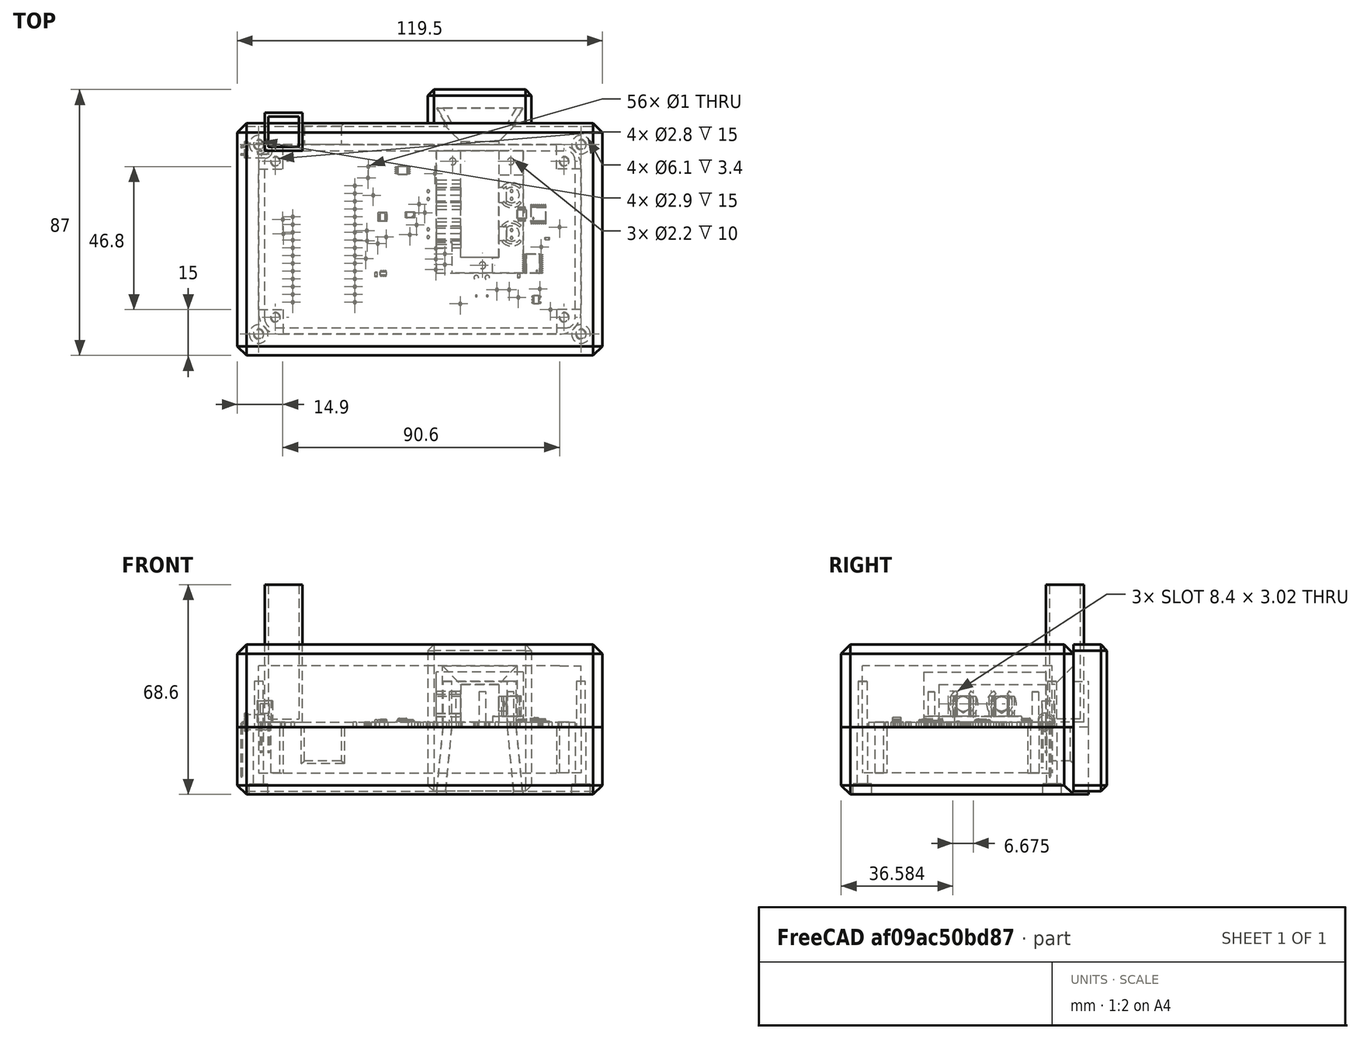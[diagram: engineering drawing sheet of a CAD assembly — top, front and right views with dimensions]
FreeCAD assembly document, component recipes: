
FREECAD ASSEMBLY — COMPONENT RECIPES ("phoenix-assembly")

This assembly document has 10 components, labeled P0..P9 below (a component is one placed body or linked part). 9 of them carry a construction recipe — the FreeCAD feature program that regenerates the part from scratch, quoted from this document or its linked companion documents; the rest are supplied as boundary geometry only. No exploded tour is included for this assembly.
COMPONENT P0 — geometry summary ("phoenix-main-board001"; no construction recipe available for this part):
  bounding box: 101.5 x 58.0 x 3.1 mm
  tessellated surface: 38,692 triangles
  volume: 9373 mm^3 (51% of its bounding box)
COMPONENT P1 — recipe-attached ("LED", modeled in this document).
Construction recipe (the document's own serialized feature program — sketch geometry with constraints, then the solid features built on it; lengths are millimeters unless a unit is written):

FEATURE [Sketcher::SketchObject] Sketch002
  ArcFitTolerance = 1e-06
  AttachmentSupport = -> [XY_Plane007]
  FullyConstrained = true
  MakeInternals = false
  MapMode = 5
  sketch-geometry (8):
    g0: LineSegment StartX=-2e-15 StartY=2.45 StartZ=0 EndX=-5.55 EndY=2.45 EndZ=0
    g1: LineSegment StartX=-5.55 StartY=2.45 StartZ=0 EndX=-5.55 EndY=3 EndZ=0
    g2: LineSegment StartX=-5.55 StartY=3 StartZ=0 EndX=-6.55 EndY=3 EndZ=0
    g3: LineSegment StartX=-6.55 StartY=3 StartZ=0 EndX=-6.55 EndY=0 EndZ=0
    g4: ArcOfCircle CenterX=0 CenterY=0 CenterZ=0 NormalX=0 NormalY=0 NormalZ=1 AngleXU=0 Radius=2.45 StartAngle=0 EndAngle=1.5708
    g5: LineSegment StartX=2.45 StartY=0 StartZ=0 EndX=-6.55 EndY=0 EndZ=0
    g6: GeomPoint X=0 Y=0 Z=0
    g7: LineSegment [constr] StartX=-5.55 StartY=2.45 StartZ=0 EndX=-5.55 EndY=0 EndZ=0
  constraints (22):
    c: PointOnObject(g0,g-2)
    c: Horizontal(g0)
    c: Coincident(g0,g1)
    c: Vertical(g1)
    c: Coincident(g1,g2)
    c: Horizontal(g2)
    c: Coincident(g2,g3)
    c: Vertical(g3)
    c: Coincident(g4,g-1)
    c: Coincident(g4,g0)
    c: Horizontal(g5)
    c: PointOnObject(g6,g5)
    c: Coincident(g6,g4)
    c: Coincident(g7,g0)
    c: Vertical(g7)
    c: DistanceX(g2,g2) = 1
    c: Coincident(g4,g5)
    c: PointOnObject(g7,g5)
    c: Coincident(g3,g5)
    c: DistanceX(g5,g5) = 9
    c: DistanceY(g3,g3) = 3
    c: DistanceY(g7,g7) = 2.45
FEATURE [PartDesign::Revolution] Revolution
  Angle = 360
  Angle2 = 60
  Axis = (1,0,0)
  Base = (0,0,0)
  Profile = -> Sketch002
  ReferenceAxis = -> X_Axis007
  Refine = true
  Reversed = true
  Suppressed = false
  Type = 0
FEATURE [Sketcher::SketchObject] Sketch003
  ArcFitTolerance = 1e-06
  AttachmentSupport = -> [Revolution]
  FullyConstrained = true
  MakeInternals = false
  MapMode = 5
  Placement = pos=(-6.55,0,0) rot=(0.57735,-0.57735,-0.57735;2.0944rad)
  sketch-geometry (9):
    g0: LineSegment StartX=-1.5 StartY=0.25 StartZ=0 EndX=-1.5 EndY=-0.25 EndZ=0
    g1: LineSegment StartX=-1.5 StartY=-0.25 StartZ=0 EndX=-1 EndY=-0.25 EndZ=0
    g2: LineSegment StartX=-1 StartY=-0.25 StartZ=0 EndX=-1 EndY=0.25 EndZ=0
    g3: LineSegment StartX=-1 StartY=0.25 StartZ=0 EndX=-1.5 EndY=0.25 EndZ=0
    g4: LineSegment StartX=1 StartY=0.25 StartZ=0 EndX=1 EndY=-0.25 EndZ=0
    g5: LineSegment StartX=1 StartY=-0.25 StartZ=0 EndX=1.5 EndY=-0.25 EndZ=0
    g6: LineSegment StartX=1.5 StartY=-0.25 StartZ=0 EndX=1.5 EndY=0.25 EndZ=0
    g7: LineSegment StartX=1.5 StartY=0.25 StartZ=0 EndX=1 EndY=0.25 EndZ=0
    g8: LineSegment [constr] StartX=-1 StartY=0.25 StartZ=0 EndX=1 EndY=0.25 EndZ=0
  constraints (25):
    c: Coincident(g0,g1)
    c: Coincident(g1,g2)
    c: Coincident(g2,g3)
    c: Coincident(g3,g0)
    c: Vertical(g0)
    c: Vertical(g2)
    c: Horizontal(g1)
    c: Horizontal(g3)
    c: Coincident(g4,g5)
    c: Coincident(g5,g6)
    c: Coincident(g6,g7)
    c: Coincident(g7,g4)
    c: Vertical(g4)
    c: Vertical(g6)
    c: Horizontal(g5)
    c: Horizontal(g7)
    c: DistanceX(g3,g3) = 0.5
    c: DistanceY(g0,g0) = 0.5
    c: Equal(g7,g3)
    c: Coincident(g8,g2)
    c: Coincident(g8,g4)
    c: Horizontal(g8)
    c: Equal(g4,g0)
    c: Symmetric(g2,g4,g-1)
    c: DistanceX(g8,g8) = 2
FEATURE [Sketcher::SketchObject] Sketch004
  ArcFitTolerance = 1e-06
  AttachmentSupport = -> [XZ_Plane007,Revolution]
  ExternalGeometry = -> [Revolution]
  FullyConstrained = true
  MakeInternals = false
  MapMode = 5
  Placement = pos=(0,0,0) rot=(1,0,0;1.5708rad)
  sketch-geometry (4):
    g0: LineSegment StartX=-6.55 StartY=-2e-16 StartZ=0 EndX=-6.65 EndY=-2e-16 EndZ=0
    g1: LineSegment StartX=-7.65 StartY=-1 StartZ=0 EndX=-7.65 EndY=-15 EndZ=0
    g2: ArcOfCircle CenterX=-6.65 CenterY=-1 CenterZ=0 NormalX=0 NormalY=0 NormalZ=1 AngleXU=0 Radius=1 StartAngle=1.5708 EndAngle=3.14159
    g3: GeomPoint [constr] X=-7.65 Y=0 Z=0
  constraints (10):
    c: Symmetric(g-3,g-3,g0)
    c: PointOnObject(g3,g-1)
    c: Vertical(g1)
    c: PointOnObject(g3,g0)
    c: PointOnObject(g3,g1)
    c: Tangent(g0,g2) = -1.5708
    c: Tangent(g1,g2) = -1.5708
    c: DistanceX(g0,g0) = 0.1
    c: DistanceX(g1,g0) = 1
    c: DistanceY(g1,g1) = 14
FEATURE [Sketcher::SketchObject] Sketch005
  ArcFitTolerance = 1e-06
  AttachmentSupport = -> [Revolution]
  ExternalGeometry = -> [Sketch003]
  FullyConstrained = true
  MakeInternals = false
  MapMode = 5
  Placement = pos=(-6.55,0,0) rot=(0.57735,-0.57735,-0.57735;2.0944rad)
  sketch-geometry (4):
    g0: LineSegment StartX=1 StartY=0.25 StartZ=0 EndX=1.5 EndY=0.25 EndZ=0
    g1: LineSegment StartX=1.5 StartY=-0.25 StartZ=0 EndX=1.5 EndY=0.25 EndZ=0
    g2: LineSegment StartX=1 StartY=0.25 StartZ=0 EndX=1 EndY=-0.25 EndZ=0
    g3: LineSegment StartX=1 StartY=-0.25 StartZ=0 EndX=1.5 EndY=-0.25 EndZ=0
  constraints (8):
    c: Coincident(g0,g-6)
    c: Coincident(g0,g-4)
    c: Coincident(g1,g-5)
    c: Coincident(g1,g0)
    c: Coincident(g2,g0)
    c: Coincident(g2,g-6)
    c: Coincident(g3,g2)
    c: Coincident(g3,g1)
FEATURE [PartDesign::AdditivePipe] AdditivePipe
  AuxilleryCurvelinear = true
  AuxillerySpineTangent = false
  BaseFeature = -> Revolution
  Binormal = (0,0,0)
  Mode = 0
  Profile = -> Sketch005
  Refine = true
  Spine = -> Sketch004
  SpineTangent = false
  Suppressed = false
  Transformation = 0
  Transition = 0
FEATURE [Sketcher::SketchObject] Sketch006
  ArcFitTolerance = 1e-06
  AttachmentSupport = -> [Revolution]
  ExternalGeometry = -> [Sketch003]
  FullyConstrained = true
  MakeInternals = false
  MapMode = 5
  Placement = pos=(-6.55,0,0) rot=(0.57735,-0.57735,-0.57735;2.0944rad)
  sketch-geometry (4):
    g0: LineSegment StartX=-1.5 StartY=0.25 StartZ=0 EndX=-1 EndY=0.25 EndZ=0
    g1: LineSegment StartX=-1 StartY=0.25 StartZ=0 EndX=-1 EndY=-0.25 EndZ=0
    g2: LineSegment StartX=-1 StartY=-0.25 StartZ=0 EndX=-1.5 EndY=-0.25 EndZ=0
    g3: LineSegment StartX=-1.5 StartY=-0.25 StartZ=0 EndX=-1.5 EndY=0.25 EndZ=0
  constraints (8):
    c: Coincident(g0,g-6)
    c: Coincident(g0,g-4)
    c: Coincident(g1,g0)
    c: Coincident(g1,g-5)
    c: Coincident(g2,g-5)
    c: Coincident(g2,g-6)
    c: Coincident(g3,g2)
    c: Coincident(g3,g0)
FEATURE [PartDesign::AdditivePipe] AdditivePipe001
  AuxilleryCurvelinear = true
  AuxillerySpineTangent = false
  BaseFeature = -> AdditivePipe
  Binormal = (0,0,0)
  Mode = 0
  Profile = -> Sketch006
  Refine = true
  Spine = -> Sketch004
  SpineTangent = false
  Suppressed = false
  Transformation = 0
  Transition = 0
FEATURE [PartDesign::Pad] Pad001
  BaseFeature = -> AdditivePipe001
  Direction = (0,0,-1)
  Length = 3
  Length2 = 10
  Profile = -> AdditivePipe001 [Face21]
  Refine = true
  Suppressed = false
  Type = 0
FEATURE [Sketcher::SketchObject] Sketch007
  ArcFitTolerance = 1e-06
  AttachmentSupport = -> [Pad001]
  ExternalGeometry = -> [Pad001]
  FullyConstrained = true
  MakeInternals = false
  MapMode = 5
  Placement = pos=(-5.55,0,0) rot=(0.57735,0.57735,0.57735;2.0944rad)
  sketch-geometry (3):
    g0: LineSegment StartX=-2.45 StartY=1.73133 StartZ=0 EndX=-2.45 EndY=-1.73133 EndZ=0
    g1: ArcOfCircle CenterX=-1.1943e-05 CenterY=5e-16 CenterZ=0 NormalX=0 NormalY=0 NormalZ=1 AngleXU=0 Radius=2.99999 StartAngle=2.52641 EndAngle=3.75678
    g2: GeomPoint X=-2.45 Y=2e-16 Z=0
  constraints (8):
    c: PointOnObject(g0,g-3)
    c: PointOnObject(g0,g-3)
    c: Vertical(g0)
    c: Coincident(g1,g0)
    c: Coincident(g1,g0)
    c: Symmetric(g0,g0,g2)
    c: PointOnObject(g2,g-4)
    c: Tangent(g1,g-3)
FEATURE [PartDesign::Pocket] Pocket
  BaseFeature = -> Pad001
  Direction = (-1,0,0)
  Length = 5
  Length2 = 5
  Profile = -> Sketch007
  ReferenceAxis = -> Sketch007 [N_Axis]
  Refine = true
  Suppressed = false
  Type = 0
FEATURE [PartDesign::Body] Body001
  AllowCompound = false
  Group = -> [Sketch002,Revolution,Sketch003,Sketch004,Sketch005,Sketch006,AdditivePipe,AdditivePipe001,Pad001,Sketch007,Pocket]
  Origin = -> Origin007
  Tip = -> Pocket
COMPONENT P2 — recipe-attached ("LED001", modeled in this document).
Construction recipe (the document's own serialized feature program — sketch geometry with constraints, then the solid features built on it; lengths are millimeters unless a unit is written):

FEATURE [Sketcher::SketchObject] Sketch008
  ArcFitTolerance = 1e-06
  AttachmentSupport = -> [XY_Plane009]
  FullyConstrained = true
  MakeInternals = false
  MapMode = 5
  sketch-geometry (8):
    g0: LineSegment StartX=-2e-15 StartY=2.45 StartZ=0 EndX=-5.55 EndY=2.45 EndZ=0
    g1: LineSegment StartX=-5.55 StartY=2.45 StartZ=0 EndX=-5.55 EndY=3 EndZ=0
    g2: LineSegment StartX=-5.55 StartY=3 StartZ=0 EndX=-6.55 EndY=3 EndZ=0
    g3: LineSegment StartX=-6.55 StartY=3 StartZ=0 EndX=-6.55 EndY=0 EndZ=0
    g4: ArcOfCircle CenterX=0 CenterY=0 CenterZ=0 NormalX=0 NormalY=0 NormalZ=1 AngleXU=0 Radius=2.45 StartAngle=0 EndAngle=1.5708
    g5: LineSegment StartX=2.45 StartY=0 StartZ=0 EndX=-6.55 EndY=0 EndZ=0
    g6: GeomPoint X=0 Y=0 Z=0
    g7: LineSegment [constr] StartX=-5.55 StartY=2.45 StartZ=0 EndX=-5.55 EndY=0 EndZ=0
  constraints (22):
    c: PointOnObject(g0,g-2)
    c: Horizontal(g0)
    c: Coincident(g0,g1)
    c: Vertical(g1)
    c: Coincident(g1,g2)
    c: Horizontal(g2)
    c: Coincident(g2,g3)
    c: Vertical(g3)
    c: Coincident(g4,g-1)
    c: Coincident(g4,g0)
    c: Horizontal(g5)
    c: PointOnObject(g6,g5)
    c: Coincident(g6,g4)
    c: Coincident(g7,g0)
    c: Vertical(g7)
    c: DistanceX(g2,g2) = 1
    c: Coincident(g4,g5)
    c: PointOnObject(g7,g5)
    c: Coincident(g3,g5)
    c: DistanceX(g5,g5) = 9
    c: DistanceY(g3,g3) = 3
    c: DistanceY(g7,g7) = 2.45
FEATURE [PartDesign::Revolution] Revolution001
  Angle = 360
  Angle2 = 60
  Axis = (1,0,0)
  Base = (0,0,0)
  Profile = -> Sketch008
  ReferenceAxis = -> X_Axis009
  Refine = true
  Reversed = true
  Suppressed = false
  Type = 0
FEATURE [Sketcher::SketchObject] Sketch009
  ArcFitTolerance = 1e-06
  AttachmentSupport = -> [Revolution001]
  FullyConstrained = true
  MakeInternals = false
  MapMode = 5
  Placement = pos=(-6.55,0,0) rot=(0.57735,-0.57735,-0.57735;2.0944rad)
  sketch-geometry (9):
    g0: LineSegment StartX=-1.5 StartY=0.25 StartZ=0 EndX=-1.5 EndY=-0.25 EndZ=0
    g1: LineSegment StartX=-1.5 StartY=-0.25 StartZ=0 EndX=-1 EndY=-0.25 EndZ=0
    g2: LineSegment StartX=-1 StartY=-0.25 StartZ=0 EndX=-1 EndY=0.25 EndZ=0
    g3: LineSegment StartX=-1 StartY=0.25 StartZ=0 EndX=-1.5 EndY=0.25 EndZ=0
    g4: LineSegment StartX=1 StartY=0.25 StartZ=0 EndX=1 EndY=-0.25 EndZ=0
    g5: LineSegment StartX=1 StartY=-0.25 StartZ=0 EndX=1.5 EndY=-0.25 EndZ=0
    g6: LineSegment StartX=1.5 StartY=-0.25 StartZ=0 EndX=1.5 EndY=0.25 EndZ=0
    g7: LineSegment StartX=1.5 StartY=0.25 StartZ=0 EndX=1 EndY=0.25 EndZ=0
    g8: LineSegment [constr] StartX=-1 StartY=0.25 StartZ=0 EndX=1 EndY=0.25 EndZ=0
  constraints (25):
    c: Coincident(g0,g1)
    c: Coincident(g1,g2)
    c: Coincident(g2,g3)
    c: Coincident(g3,g0)
    c: Vertical(g0)
    c: Vertical(g2)
    c: Horizontal(g1)
    c: Horizontal(g3)
    c: Coincident(g4,g5)
    c: Coincident(g5,g6)
    c: Coincident(g6,g7)
    c: Coincident(g7,g4)
    c: Vertical(g4)
    c: Vertical(g6)
    c: Horizontal(g5)
    c: Horizontal(g7)
    c: DistanceX(g3,g3) = 0.5
    c: DistanceY(g0,g0) = 0.5
    c: Equal(g7,g3)
    c: Coincident(g8,g2)
    c: Coincident(g8,g4)
    c: Horizontal(g8)
    c: Equal(g4,g0)
    c: Symmetric(g2,g4,g-1)
    c: DistanceX(g8,g8) = 2
FEATURE [Sketcher::SketchObject] Sketch010
  ArcFitTolerance = 1e-06
  AttachmentSupport = -> [XZ_Plane009,Revolution001]
  ExternalGeometry = -> [Revolution001]
  FullyConstrained = true
  MakeInternals = false
  MapMode = 5
  Placement = pos=(0,0,0) rot=(1,0,0;1.5708rad)
  sketch-geometry (4):
    g0: LineSegment StartX=-6.55 StartY=-2e-16 StartZ=0 EndX=-6.65 EndY=-2e-16 EndZ=0
    g1: LineSegment StartX=-7.65 StartY=-1 StartZ=0 EndX=-7.65 EndY=-15 EndZ=0
    g2: ArcOfCircle CenterX=-6.65 CenterY=-1 CenterZ=0 NormalX=0 NormalY=0 NormalZ=1 AngleXU=0 Radius=1 StartAngle=1.5708 EndAngle=3.14159
    g3: GeomPoint [constr] X=-7.65 Y=0 Z=0
  constraints (10):
    c: Symmetric(g-3,g-3,g0)
    c: PointOnObject(g3,g-1)
    c: Vertical(g1)
    c: PointOnObject(g3,g0)
    c: PointOnObject(g3,g1)
    c: Tangent(g0,g2) = -1.5708
    c: Tangent(g1,g2) = -1.5708
    c: DistanceX(g0,g0) = 0.1
    c: DistanceX(g1,g0) = 1
    c: DistanceY(g1,g1) = 14
FEATURE [Sketcher::SketchObject] Sketch011
  ArcFitTolerance = 1e-06
  AttachmentSupport = -> [Revolution001]
  ExternalGeometry = -> [Sketch009]
  FullyConstrained = true
  MakeInternals = false
  MapMode = 5
  Placement = pos=(-6.55,0,0) rot=(0.57735,-0.57735,-0.57735;2.0944rad)
  sketch-geometry (4):
    g0: LineSegment StartX=1 StartY=0.25 StartZ=0 EndX=1.5 EndY=0.25 EndZ=0
    g1: LineSegment StartX=1.5 StartY=-0.25 StartZ=0 EndX=1.5 EndY=0.25 EndZ=0
    g2: LineSegment StartX=1 StartY=0.25 StartZ=0 EndX=1 EndY=-0.25 EndZ=0
    g3: LineSegment StartX=1 StartY=-0.25 StartZ=0 EndX=1.5 EndY=-0.25 EndZ=0
  constraints (8):
    c: Coincident(g0,g-6)
    c: Coincident(g0,g-4)
    c: Coincident(g1,g-5)
    c: Coincident(g1,g0)
    c: Coincident(g2,g0)
    c: Coincident(g2,g-6)
    c: Coincident(g3,g2)
    c: Coincident(g3,g1)
FEATURE [PartDesign::AdditivePipe] AdditivePipe002
  AuxilleryCurvelinear = true
  AuxillerySpineTangent = false
  BaseFeature = -> Revolution001
  Binormal = (0,0,0)
  Mode = 0
  Profile = -> Sketch011
  Refine = true
  Spine = -> Sketch010
  SpineTangent = false
  Suppressed = false
  Transformation = 0
  Transition = 0
FEATURE [Sketcher::SketchObject] Sketch012
  ArcFitTolerance = 1e-06
  AttachmentSupport = -> [Revolution001]
  ExternalGeometry = -> [Sketch009]
  FullyConstrained = true
  MakeInternals = false
  MapMode = 5
  Placement = pos=(-6.55,0,0) rot=(0.57735,-0.57735,-0.57735;2.0944rad)
  sketch-geometry (4):
    g0: LineSegment StartX=-1.5 StartY=0.25 StartZ=0 EndX=-1 EndY=0.25 EndZ=0
    g1: LineSegment StartX=-1 StartY=0.25 StartZ=0 EndX=-1 EndY=-0.25 EndZ=0
    g2: LineSegment StartX=-1 StartY=-0.25 StartZ=0 EndX=-1.5 EndY=-0.25 EndZ=0
    g3: LineSegment StartX=-1.5 StartY=-0.25 StartZ=0 EndX=-1.5 EndY=0.25 EndZ=0
  constraints (8):
    c: Coincident(g0,g-6)
    c: Coincident(g0,g-4)
    c: Coincident(g1,g0)
    c: Coincident(g1,g-5)
    c: Coincident(g2,g-5)
    c: Coincident(g2,g-6)
    c: Coincident(g3,g2)
    c: Coincident(g3,g0)
FEATURE [PartDesign::AdditivePipe] AdditivePipe003
  AuxilleryCurvelinear = true
  AuxillerySpineTangent = false
  BaseFeature = -> AdditivePipe002
  Binormal = (0,0,0)
  Mode = 0
  Profile = -> Sketch012
  Refine = true
  Spine = -> Sketch010
  SpineTangent = false
  Suppressed = false
  Transformation = 0
  Transition = 0
FEATURE [PartDesign::Pad] Pad002
  BaseFeature = -> AdditivePipe003
  Direction = (0,0,-1)
  Length = 3
  Length2 = 10
  Profile = -> AdditivePipe003 [Face21]
  Refine = true
  Suppressed = false
  Type = 0
FEATURE [Sketcher::SketchObject] Sketch013
  ArcFitTolerance = 1e-06
  AttachmentSupport = -> [Pad002]
  ExternalGeometry = -> [Pad002]
  FullyConstrained = true
  MakeInternals = false
  MapMode = 5
  Placement = pos=(-5.55,0,0) rot=(0.57735,0.57735,0.57735;2.0944rad)
  sketch-geometry (3):
    g0: LineSegment StartX=-2.45 StartY=1.73133 StartZ=0 EndX=-2.45 EndY=-1.73133 EndZ=0
    g1: ArcOfCircle CenterX=-1.1943e-05 CenterY=5e-16 CenterZ=0 NormalX=0 NormalY=0 NormalZ=1 AngleXU=0 Radius=2.99999 StartAngle=2.52641 EndAngle=3.75678
    g2: GeomPoint X=-2.45 Y=2e-16 Z=0
  constraints (8):
    c: PointOnObject(g0,g-3)
    c: PointOnObject(g0,g-3)
    c: Vertical(g0)
    c: Coincident(g1,g0)
    c: Coincident(g1,g0)
    c: Symmetric(g0,g0,g2)
    c: PointOnObject(g2,g-4)
    c: Tangent(g1,g-3)
FEATURE [PartDesign::Pocket] Pocket001
  BaseFeature = -> Pad002
  Direction = (-1,0,0)
  Length = 5
  Length2 = 5
  Profile = -> Sketch013
  ReferenceAxis = -> Sketch013 [N_Axis]
  Refine = true
  Suppressed = false
  Type = 0
FEATURE [PartDesign::Body] Body002
  AllowCompound = false
  Group = -> [Sketch008,Revolution001,Sketch009,Sketch010,Sketch011,Sketch012,AdditivePipe002,AdditivePipe003,Pad002,Sketch013,Pocket001]
  Origin = -> Origin009
  Tip = -> Pocket001
COMPONENT P3 — recipe-attached ("Photodiode", modeled in this document).
Construction recipe (the document's own serialized feature program — sketch geometry with constraints, then the solid features built on it; lengths are millimeters unless a unit is written):

FEATURE [Sketcher::SketchObject] Sketch014
  ArcFitTolerance = 1e-06
  AttachmentSupport = -> [XY_Plane011]
  FullyConstrained = true
  MakeInternals = false
  MapMode = 5
  sketch-geometry (2):
    g0: ArcOfCircle CenterX=0 CenterY=0 CenterZ=0 NormalX=0 NormalY=0 NormalZ=1 AngleXU=0 Radius=2.5 StartAngle=5.78253 EndAngle=9.92543
    g1: LineSegment StartX=-2.19317 StartY=-1.2 StartZ=0 EndX=2.19317 EndY=-1.2 EndZ=0
  constraints (6):
    c: Coincident(g0,g-1)
    c: Diameter(g0) = 5
    c: Horizontal(g1)
    c: Distance(g0,g1) = -1.3
    c: Coincident(g0,g1)
    c: Coincident(g0,g1)
FEATURE [PartDesign::Pad] Pad003
  Direction = (0,0,1)
  Length = 7
  Length2 = 10
  Profile = -> Sketch014
  ReferenceAxis = -> Sketch014 [N_Axis]
  Refine = true
  Suppressed = false
  Type = 0
FEATURE [Sketcher::SketchObject] Sketch015
  ArcFitTolerance = 1e-06
  AttachmentSupport = -> [Pad003]
  FullyConstrained = true
  MakeInternals = false
  MapMode = 5
  Placement = pos=(0,0,0) rot=(1,0,0;3.14159rad)
  sketch-geometry (10):
    g0: LineSegment StartX=-1.5 StartY=0.25 StartZ=0 EndX=-1.5 EndY=-0.25 EndZ=0
    g1: LineSegment StartX=-1.5 StartY=-0.25 StartZ=0 EndX=-1 EndY=-0.25 EndZ=0
    g2: LineSegment StartX=-1 StartY=-0.25 StartZ=0 EndX=-1 EndY=0.25 EndZ=0
    g3: LineSegment StartX=-1 StartY=0.25 StartZ=0 EndX=-1.5 EndY=0.25 EndZ=0
    g4: LineSegment StartX=1 StartY=0.25 StartZ=0 EndX=1 EndY=-0.25 EndZ=0
    g5: LineSegment StartX=1 StartY=-0.25 StartZ=0 EndX=1.5 EndY=-0.25 EndZ=0
    g6: LineSegment StartX=1.5 StartY=-0.25 StartZ=0 EndX=1.5 EndY=0.25 EndZ=0
    g7: LineSegment StartX=1.5 StartY=0.25 StartZ=0 EndX=1 EndY=0.25 EndZ=0
    g8: GeomPoint X=-1 Y=0 Z=0
    g9: GeomPoint X=1 Y=0 Z=0
  constraints (25):
    c: Coincident(g0,g1)
    c: Coincident(g1,g2)
    c: Coincident(g2,g3)
    c: Coincident(g3,g0)
    c: Vertical(g0)
    c: Vertical(g2)
    c: Horizontal(g1)
    c: Horizontal(g3)
    c: Coincident(g4,g5)
    c: Coincident(g5,g6)
    c: Coincident(g6,g7)
    c: Coincident(g7,g4)
    c: Vertical(g4)
    c: Vertical(g6)
    c: Horizontal(g5)
    c: Horizontal(g7)
    c: Equal(g3,g2)
    c: Equal(g7,g6)
    c: Symmetric(g2,g2,g8)
    c: Symmetric(g4,g4,g9)
    c: Symmetric(g9,g8,g-1)
    c: PointOnObject(g9,g-1)
    c: DistanceX(g3,g3) = 0.5
    c: Equal(g3,g7)
    c: Distance(g4,g2) = 2
FEATURE [PartDesign::Pad] Pad004
  BaseFeature = -> Pad003
  Direction = (0,0,-1)
  Length = 10
  Length2 = 10
  Profile = -> Sketch015
  ReferenceAxis = -> Sketch015 [N_Axis]
  Refine = true
  Suppressed = false
  Type = 0
FEATURE [Sketcher::SketchObject] Sketch016
  ArcFitTolerance = 1e-06
  AttachmentSupport = -> [Pad004]
  ExternalGeometry = -> [Pad004]
  FullyConstrained = true
  MakeInternals = false
  MapMode = 5
  Placement = pos=(0,-1.2,0) rot=(1,0,0;1.5708rad)
  sketch-geometry (5):
    g0: LineSegment StartX=-1.5 StartY=6 StartZ=0 EndX=-1.5 EndY=3 EndZ=0
    g1: LineSegment StartX=-1.5 StartY=3 StartZ=0 EndX=1.5 EndY=3 EndZ=0
    g2: LineSegment StartX=1.5 StartY=3 StartZ=0 EndX=1.5 EndY=6 EndZ=0
    g3: LineSegment StartX=1.5 StartY=6 StartZ=0 EndX=-1.5 EndY=6 EndZ=0
    g4: GeomPoint X=0 Y=6 Z=0
  constraints (13):
    c: Coincident(g0,g1)
    c: Coincident(g1,g2)
    c: Coincident(g2,g3)
    c: Coincident(g3,g0)
    c: Vertical(g0)
    c: Vertical(g2)
    c: Horizontal(g1)
    c: Horizontal(g3)
    c: Symmetric(g3,g3,g4)
    c: PointOnObject(g4,g-2)
    c: DistanceX(g3,g3) = 3
    c: Equal(g2,g3)
    c: Distance(g-3,g3) = 1
FEATURE [PartDesign::Pocket] Pocket002
  BaseFeature = -> Pad004
  Direction = (0,1,-2e-16)
  Length = 0.1
  Length2 = 5
  Profile = -> Sketch016
  ReferenceAxis = -> Sketch016 [N_Axis]
  Refine = true
  Suppressed = false
  Type = 0
FEATURE [PartDesign::Body] Body003
  AllowCompound = false
  Group = -> [Sketch014,Pad003,Sketch015,Pad004,Sketch016,Pocket002]
  Origin = -> Origin011
  Tip = -> Pocket002
COMPONENT P4 — recipe-attached ("Photodiode001", modeled in this document).
Construction recipe (the document's own serialized feature program — sketch geometry with constraints, then the solid features built on it; lengths are millimeters unless a unit is written):

FEATURE [Sketcher::SketchObject] Sketch017
  ArcFitTolerance = 1e-06
  AttachmentSupport = -> [XY_Plane013]
  FullyConstrained = true
  MakeInternals = false
  MapMode = 5
  sketch-geometry (2):
    g0: ArcOfCircle CenterX=0 CenterY=0 CenterZ=0 NormalX=0 NormalY=0 NormalZ=1 AngleXU=0 Radius=2.5 StartAngle=5.78253 EndAngle=9.92543
    g1: LineSegment StartX=-2.19317 StartY=-1.2 StartZ=0 EndX=2.19317 EndY=-1.2 EndZ=0
  constraints (6):
    c: Coincident(g0,g-1)
    c: Diameter(g0) = 5
    c: Horizontal(g1)
    c: Distance(g0,g1) = -1.3
    c: Coincident(g0,g1)
    c: Coincident(g0,g1)
FEATURE [PartDesign::Pad] Pad005
  Direction = (0,0,1)
  Length = 7
  Length2 = 10
  Profile = -> Sketch017
  ReferenceAxis = -> Sketch017 [N_Axis]
  Refine = true
  Suppressed = false
  Type = 0
FEATURE [Sketcher::SketchObject] Sketch018
  ArcFitTolerance = 1e-06
  AttachmentSupport = -> [Pad005]
  FullyConstrained = true
  MakeInternals = false
  MapMode = 5
  Placement = pos=(0,0,0) rot=(1,0,0;3.14159rad)
  sketch-geometry (10):
    g0: LineSegment StartX=-1.5 StartY=0.25 StartZ=0 EndX=-1.5 EndY=-0.25 EndZ=0
    g1: LineSegment StartX=-1.5 StartY=-0.25 StartZ=0 EndX=-1 EndY=-0.25 EndZ=0
    g2: LineSegment StartX=-1 StartY=-0.25 StartZ=0 EndX=-1 EndY=0.25 EndZ=0
    g3: LineSegment StartX=-1 StartY=0.25 StartZ=0 EndX=-1.5 EndY=0.25 EndZ=0
    g4: LineSegment StartX=1 StartY=0.25 StartZ=0 EndX=1 EndY=-0.25 EndZ=0
    g5: LineSegment StartX=1 StartY=-0.25 StartZ=0 EndX=1.5 EndY=-0.25 EndZ=0
    g6: LineSegment StartX=1.5 StartY=-0.25 StartZ=0 EndX=1.5 EndY=0.25 EndZ=0
    g7: LineSegment StartX=1.5 StartY=0.25 StartZ=0 EndX=1 EndY=0.25 EndZ=0
    g8: GeomPoint X=-1 Y=0 Z=0
    g9: GeomPoint X=1 Y=0 Z=0
  constraints (25):
    c: Coincident(g0,g1)
    c: Coincident(g1,g2)
    c: Coincident(g2,g3)
    c: Coincident(g3,g0)
    c: Vertical(g0)
    c: Vertical(g2)
    c: Horizontal(g1)
    c: Horizontal(g3)
    c: Coincident(g4,g5)
    c: Coincident(g5,g6)
    c: Coincident(g6,g7)
    c: Coincident(g7,g4)
    c: Vertical(g4)
    c: Vertical(g6)
    c: Horizontal(g5)
    c: Horizontal(g7)
    c: Equal(g3,g2)
    c: Equal(g7,g6)
    c: Symmetric(g2,g2,g8)
    c: Symmetric(g4,g4,g9)
    c: Symmetric(g9,g8,g-1)
    c: PointOnObject(g9,g-1)
    c: DistanceX(g3,g3) = 0.5
    c: Equal(g3,g7)
    c: Distance(g4,g2) = 2
FEATURE [PartDesign::Pad] Pad006
  BaseFeature = -> Pad005
  Direction = (0,0,-1)
  Length = 10
  Length2 = 10
  Profile = -> Sketch018
  ReferenceAxis = -> Sketch018 [N_Axis]
  Refine = true
  Suppressed = false
  Type = 0
FEATURE [Sketcher::SketchObject] Sketch019
  ArcFitTolerance = 1e-06
  AttachmentSupport = -> [Pad006]
  ExternalGeometry = -> [Pad006]
  FullyConstrained = true
  MakeInternals = false
  MapMode = 5
  Placement = pos=(0,-1.2,0) rot=(1,0,0;1.5708rad)
  sketch-geometry (5):
    g0: LineSegment StartX=-1.5 StartY=6 StartZ=0 EndX=-1.5 EndY=3 EndZ=0
    g1: LineSegment StartX=-1.5 StartY=3 StartZ=0 EndX=1.5 EndY=3 EndZ=0
    g2: LineSegment StartX=1.5 StartY=3 StartZ=0 EndX=1.5 EndY=6 EndZ=0
    g3: LineSegment StartX=1.5 StartY=6 StartZ=0 EndX=-1.5 EndY=6 EndZ=0
    g4: GeomPoint X=0 Y=6 Z=0
  constraints (13):
    c: Coincident(g0,g1)
    c: Coincident(g1,g2)
    c: Coincident(g2,g3)
    c: Coincident(g3,g0)
    c: Vertical(g0)
    c: Vertical(g2)
    c: Horizontal(g1)
    c: Horizontal(g3)
    c: Symmetric(g3,g3,g4)
    c: PointOnObject(g4,g-2)
    c: DistanceX(g3,g3) = 3
    c: Equal(g2,g3)
    c: Distance(g-3,g3) = 1
FEATURE [PartDesign::Pocket] Pocket003
  BaseFeature = -> Pad006
  Direction = (0,1,-2e-16)
  Length = 0.1
  Length2 = 5
  Profile = -> Sketch019
  ReferenceAxis = -> Sketch019 [N_Axis]
  Refine = true
  Suppressed = false
  Type = 0
FEATURE [PartDesign::Body] Body004
  AllowCompound = false
  Group = -> [Sketch017,Pad005,Sketch018,Pad006,Sketch019,Pocket003]
  Origin = -> Origin013
  Tip = -> Pocket003
COMPONENT P5 — recipe-attached ("Cuvette", modeled in this document).
Construction recipe (the document's own serialized feature program — sketch geometry with constraints, then the solid features built on it; lengths are millimeters unless a unit is written):

FEATURE [Sketcher::SketchObject] Sketch020
  ArcFitTolerance = 1e-06
  AttachmentSupport = -> [XY_Plane015]
  FullyConstrained = true
  MakeInternals = false
  MapMode = 5
  sketch-geometry (4):
    g0: LineSegment StartX=0 StartY=0 StartZ=0 EndX=12.4 EndY=0 EndZ=0
    g1: LineSegment StartX=12.4 StartY=0 StartZ=0 EndX=12.4 EndY=12.4 EndZ=0
    g2: LineSegment StartX=12.4 StartY=12.4 StartZ=0 EndX=0 EndY=12.4 EndZ=0
    g3: LineSegment StartX=0 StartY=12.4 StartZ=0 EndX=0 EndY=0 EndZ=0
  constraints (11):
    c: Coincident(g0,g1)
    c: Coincident(g1,g2)
    c: Coincident(g2,g3)
    c: Coincident(g3,g0)
    c: Horizontal(g0)
    c: Horizontal(g2)
    c: Vertical(g1)
    c: Vertical(g3)
    c: Coincident(g0,g-1)
    c: DistanceX(g2,g2) = 12.4
    c: DistanceY(g3,g3) = 12.4
FEATURE [PartDesign::Pad] Pad007
  Direction = (0,0,1)
  Length = 45
  Length2 = 10
  Profile = -> Sketch020
  ReferenceAxis = -> Sketch020 [N_Axis]
  Refine = true
  Suppressed = false
  Type = 0
FEATURE [Sketcher::SketchObject] Sketch021
  ArcFitTolerance = 1e-06
  AttachmentSupport = -> [Pad007]
  ExternalGeometry = -> [Pad007]
  FullyConstrained = true
  MakeInternals = false
  MapMode = 5
  Placement = pos=(0,0,45) rot=(0,0,1;0rad)
  sketch-geometry (5):
    g0: LineSegment StartX=1.2 StartY=11.2 StartZ=0 EndX=1.2 EndY=1.2 EndZ=0
    g1: LineSegment StartX=1.2 StartY=1.2 StartZ=0 EndX=11.2 EndY=1.2 EndZ=0
    g2: LineSegment StartX=11.2 StartY=1.2 StartZ=0 EndX=11.2 EndY=11.2 EndZ=0
    g3: LineSegment StartX=11.2 StartY=11.2 StartZ=0 EndX=1.2 EndY=11.2 EndZ=0
    g4: GeomPoint X=6.2 Y=6.2 Z=0
  constraints (12):
    c: Coincident(g0,g1)
    c: Coincident(g1,g2)
    c: Coincident(g2,g3)
    c: Coincident(g3,g0)
    c: Vertical(g0)
    c: Vertical(g2)
    c: Horizontal(g1)
    c: Horizontal(g3)
    c: Symmetric(g0,g1,g4)
    c: Symmetric(g-3,g-1,g4)
    c: DistanceX(g3,g3) = 10
    c: DistanceY(g2,g2) = 10
FEATURE [PartDesign::Pocket] Pocket004
  BaseFeature = -> Pad007
  Direction = (0,0,-1)
  Length = 44
  Length2 = 5
  Profile = -> Sketch021
  ReferenceAxis = -> Sketch021 [N_Axis]
  Refine = true
  Suppressed = false
  Type = 0
FEATURE [PartDesign::Body] Body005  label="cuvette"
  AllowCompound = false
  Group = -> [Sketch020,Pad007,Sketch021,Pocket004]
  Origin = -> Origin015
  Tip = -> Pocket004
COMPONENT P6 — recipe-attached ("Shroud", modeled in this document).
Construction recipe (the document's own serialized feature program — sketch geometry with constraints, then the solid features built on it; lengths are millimeters unless a unit is written):

FEATURE [PartDesign::SubShapeBinder] Binder  label="Cuvette001"
  BindCopyOnChange = 0
  BindMode = 0
  ClaimChildren = false
  Context = -> Assembly [Part010.Body.Binder.]
  Fuse = false
  MakeFace = true
  OffsetFill = false
  OffsetIntersection = false
  OffsetJoinType = 0
  OffsetOpenResult = false
  PartialLoad = false
  Refine = true
  Relative = true
  Support = -> [Part009[Body005.Pocket004.Face1]]
  _Version = 2
FEATURE [PartDesign::SubShapeBinder] Binder001  label="PCB"
  BindCopyOnChange = 0
  BindMode = 0
  ClaimChildren = false
  Context = -> Assembly [Part010.Body.Binder001.]
  Fuse = false
  MakeFace = true
  OffsetFill = false
  OffsetIntersection = false
  OffsetJoinType = 0
  OffsetOpenResult = false
  PartialLoad = false
  Refine = true
  Relative = true
  Support = -> [Board_bfa0[Pcb_bfa0.Face84]]
  _Version = 2
FEATURE [PartDesign::SubShapeBinder] Binder002  label="LED1"
  BindCopyOnChange = 0
  BindMode = 0
  ClaimChildren = false
  Context = -> Assembly [Part010.Body.Binder002.]
  Fuse = false
  MakeFace = true
  OffsetFill = false
  OffsetIntersection = false
  OffsetJoinType = 0
  OffsetOpenResult = false
  PartialLoad = false
  Refine = true
  Relative = true
  Support = -> [Part[Body001.Pocket.Edge4]]
  _Version = 2
FEATURE [PartDesign::SubShapeBinder] Binder003  label="LED2"
  BindCopyOnChange = 0
  BindMode = 0
  ClaimChildren = false
  Context = -> Assembly [Part010.Body.Binder003.]
  Fuse = false
  MakeFace = true
  OffsetFill = false
  OffsetIntersection = false
  OffsetJoinType = 0
  OffsetOpenResult = false
  PartialLoad = false
  Refine = true
  Relative = true
  Support = -> [Part006[Body002.Pocket001.Edge4]]
  _Version = 2
FEATURE [PartDesign::SubShapeBinder] Binder004
  BindCopyOnChange = 0
  BindMode = 0
  ClaimChildren = false
  Context = -> Assembly [Part010.Body.Binder004.]
  Fuse = false
  MakeFace = true
  OffsetFill = false
  OffsetIntersection = false
  OffsetJoinType = 0
  OffsetOpenResult = false
  PartialLoad = false
  Refine = true
  Relative = true
  Support = -> [Part008[Body004.Pocket003.Face2]]
  _Version = 2
FEATURE [Sketcher::SketchObject] Sketch
  ArcFitTolerance = 1e-06
  AttachmentSupport = -> [Binder]
  ExternalGeometry = -> [Binder]
  FullyConstrained = true
  MakeInternals = false
  MapMode = 5
  Placement = pos=(0,0,12.4) rot=(0,0,1;0rad)
  sketch-geometry (6):
    g0: LineSegment StartX=56.1806 StartY=-40.0057 StartZ=0 EndX=84.5806 EndY=-40.0057 EndZ=0
    g1: LineSegment StartX=84.5806 StartY=-40.0057 StartZ=0 EndX=84.5806 EndY=0 EndZ=0
    g2: LineSegment StartX=84.5806 StartY=0 StartZ=0 EndX=56.1806 EndY=0 EndZ=0
    g3: LineSegment StartX=56.1806 StartY=0 StartZ=0 EndX=56.1806 EndY=-40.0057 EndZ=0
    g4: GeomPoint X=76.5806 Y=0 Z=0
    g5: GeomPoint X=64.1806 Y=0 Z=0
  constraints (16):
    c: Coincident(g0,g1)
    c: Coincident(g1,g2)
    c: Coincident(g2,g3)
    c: Coincident(g3,g0)
    c: Horizontal(g0)
    c: Horizontal(g2)
    c: Vertical(g1)
    c: Vertical(g3)
    c: PointOnObject(g1,g-1)
    c: PointOnObject(g4,g-5)
    c: PointOnObject(g5,g2)
    c: PointOnObject(g4,g2)
    c: PointOnObject(g5,g-3)
    c: DistanceX(g4,g1) = 8
    c: Distance(g5,g2) = 8
    c: Distance(g-4,g0) = 5
FEATURE [PartDesign::Pad] Pad
  Direction = (0,0,1)
  Length = 4
  Length2 = 10
  Profile = -> Sketch
  ReferenceAxis = -> Sketch [N_Axis]
  Refine = true
  Suppressed = false
  Type = 0
FEATURE [Sketcher::SketchObject] Sketch022
  ArcFitTolerance = 1e-06
  AttachmentSupport = -> [Pad]
  ExternalGeometry = -> [Binder,Pad]
  FullyConstrained = false
  MakeInternals = false
  MapMode = 5
  Placement = pos=(0,0,12.4) rot=(1,0,0;3.14159rad)
  sketch-geometry (9):
    g0: LineSegment StartX=56.1806 StartY=40.0057 StartZ=0 EndX=56.1806 EndY=0 EndZ=0
    g1: LineSegment StartX=56.1806 StartY=0 StartZ=0 EndX=64.1806 EndY=0 EndZ=0
    g2: LineSegment StartX=84.5806 StartY=0 StartZ=0 EndX=84.5806 EndY=40.0057 EndZ=0
    g3: LineSegment StartX=84.5806 StartY=40.0057 StartZ=0 EndX=56.1806 EndY=40.0057 EndZ=0
    g4: LineSegment StartX=76.6127 StartY=34.9943 StartZ=0 EndX=64.1806 EndY=34.9943 EndZ=0
    g5: LineSegment StartX=64.1806 StartY=34.9943 StartZ=0 EndX=64.1806 EndY=0 EndZ=0
    g6: LineSegment StartX=76.5806 StartY=0 StartZ=0 EndX=76.6127 EndY=0 EndZ=0
    g7: LineSegment StartX=76.6127 StartY=0 StartZ=0 EndX=76.6127 EndY=34.9943 EndZ=0
    g8: LineSegment StartX=76.5806 StartY=0 StartZ=0 EndX=84.5806 EndY=0 EndZ=0
  constraints (22):
    c: Coincident(g0,g1)
    c: Coincident(g8,g2)
    c: Coincident(g2,g3)
    c: Coincident(g3,g0)
    c: Vertical(g0)
    c: Vertical(g2)
    c: Horizontal(g1)
    c: Horizontal(g3)
    c: Coincident(g0,g-7)
    c: Coincident(g8,g-9)
    c: Coincident(g4,g5)
    c: Coincident(g6,g7)
    c: Coincident(g7,g4)
    c: Horizontal(g4)
    c: Horizontal(g6)
    c: Vertical(g5)
    c: Vertical(g7)
    c: Coincident(g4,g-5)
    c: PointOnObject(g5,g-3)
    c: Coincident(g1,g5)
    c: PointOnObject(g8,g-4)
    c: PointOnObject(g6,g8)
FEATURE [PartDesign::Pad] Pad008
  BaseFeature = -> Pad
  Direction = (0,0,-1)
  Length = 10
  Length2 = 10
  Profile = -> Sketch022
  ReferenceAxis = -> Sketch022 [N_Axis]
  Refine = true
  Suppressed = false
  Type = 3
  UpToFace = -> Binder001 [Face1]
FEATURE [Sketcher::SketchObject] Sketch023
  ArcFitTolerance = 1e-06
  AttachmentSupport = -> [Pad008]
  ExternalGeometry = -> [Binder003]
  FullyConstrained = false
  MakeInternals = false
  MapMode = 5
  Placement = pos=(56.1806,0,0) rot=(0.57735,-0.57735,-0.57735;2.0944rad)
  sketch-geometry (19):
    g0: ArcOfCircle CenterX=27.0787 CenterY=6 CenterZ=0 NormalX=0 NormalY=0 NormalZ=1 AngleXU=0 Radius=2.45 StartAngle=5.32325 EndAngle=10.3847
    g1: LineSegment StartX=25.6735 StartY=3.99308 StartZ=0 EndX=27.0787 EndY=3.0091 EndZ=0
    g2: LineSegment StartX=27.0787 StartY=3.0091 StartZ=0 EndX=28.484 EndY=3.99308 EndZ=0
    g3: LineSegment [constr] StartX=25.6735 StartY=3.99308 StartZ=0 EndX=28.484 EndY=3.99308 EndZ=0
    g4: Circle [constr] CenterX=27.0787 CenterY=6 CenterZ=0 NormalX=0 NormalY=0 NormalZ=1 AngleXU=0 Radius=3.65
    g5: Circle [constr] CenterX=27.0787 CenterY=6 CenterZ=0 NormalX=0 NormalY=0 NormalZ=1 AngleXU=0 Radius=4.85
    g6: ArcOfCircle CenterX=27.0787 CenterY=6 CenterZ=0 NormalX=0 NormalY=0 NormalZ=1 AngleXU=0 Radius=3.65 StartAngle=5.23599 EndAngle=7.33038
    g7: ArcOfCircle CenterX=27.0787 CenterY=6 CenterZ=0 NormalX=0 NormalY=0 NormalZ=1 AngleXU=0 Radius=4.85 StartAngle=5.23599 EndAngle=7.33038
    g8: LineSegment [constr] StartX=27.0787 StartY=6 StartZ=0 EndX=29.5037 EndY=1.79978 EndZ=0
    g9: LineSegment [constr] StartX=27.0787 StartY=6 StartZ=0 EndX=24.6537 EndY=1.79978 EndZ=0
    g10: LineSegment [constr] StartX=27.0787 StartY=6 StartZ=0 EndX=27.0787 EndY=1.15 EndZ=0
    g11: LineSegment [constr] StartX=27.0787 StartY=6 StartZ=0 EndX=29.5037 EndY=10.2002 EndZ=0
    g12: LineSegment [constr] StartX=27.0787 StartY=6 StartZ=0 EndX=24.6537 EndY=10.2002 EndZ=0
    g13: LineSegment StartX=29.5037 StartY=1.79978 StartZ=0 EndX=28.9037 EndY=2.83901 EndZ=0
    g14: LineSegment StartX=29.5037 StartY=10.2002 StartZ=0 EndX=28.9037 EndY=9.16099 EndZ=0
    g15: LineSegment StartX=24.6537 StartY=10.2002 StartZ=0 EndX=25.2537 EndY=9.16099 EndZ=0
    g16: LineSegment StartX=24.6537 StartY=1.79978 StartZ=0 EndX=25.2537 EndY=2.83901 EndZ=0
    g17: ArcOfCircle CenterX=27.0787 CenterY=6 CenterZ=0 NormalX=0 NormalY=0 NormalZ=1 AngleXU=0 Radius=3.65 StartAngle=2.0944 EndAngle=4.18879
    g18: ArcOfCircle CenterX=27.0787 CenterY=6 CenterZ=0 NormalX=0 NormalY=0 NormalZ=1 AngleXU=0 Radius=4.85 StartAngle=2.0944 EndAngle=4.18879
  constraints (51):
    c: Coincident(g0,g-3)
    c: Coincident(g2,g1)
    c: Vertical(g1,g0)
    c: Coincident(g3,g1)
    c: Coincident(g3,g2)
    c: Angle(g1,g3) = 0.610865
    c: Tangent(g0,g1) = -1.5708
    c: Tangent(g0,g2) = -1.5708
    c: Radius(g0) = 2.45
    c: Coincident(g4,g0)
    c: Coincident(g5,g0)
    c: Distance(g0,g4) = 1.2
    c: Distance(g5,g4) = 1.2
    c: Coincident(g6,g0)
    c: Coincident(g7,g0)
    c: Equal(g4,g6)
    c: Equal(g7,g5)
    c: Coincident(g8,g0)
    c: Coincident(g9,g0)
    c: Coincident(g10,g0)
    c: Vertical(g10)
    c: Coincident(g11,g0)
    c: Coincident(g12,g0)
    c: PointOnObject(g12,g18)
    c: Angle(g9,g10) = 0.523599
    c: Angle(g10,g8) = 0.523599
    c: Angle(g12,g10) = 2.61799
    c: Angle(g10,g11) = 2.61799
    c: Coincident(g13,g8)
    c: Coincident(g14,g11)
    c: PointOnObject(g14,g6)
    c: Coincident(g15,g12)
    c: PointOnObject(g15,g17)
    c: Coincident(g16,g9)
    c: PointOnObject(g16,g17)
    c: PointOnObject(g16,g9)
    c: PointOnObject(g13,g8)
    c: PointOnObject(g14,g11)
    c: PointOnObject(g15,g12)
    c: Coincident(g7,g8)
    c: Coincident(g6,g13)
    c: Coincident(g18,g9)
    c: PointOnObject(g17,g9)
    c: Equal(g6,g17)
    c: PointOnObject(g6,g11)
    c: PointOnObject(g17,g15)
    c: Coincident(g6,g17)
    c: Equal(g7,g18)
    c: Coincident(g7,g11)
    c: PointOnObject(g18,g12)
    c: Coincident(g7,g18)
FEATURE [Sketcher::SketchObject] Sketch024
  ArcFitTolerance = 1e-06
  AttachmentSupport = -> [Pad008]
  ExternalGeometry = -> [Binder002,Binder003]
  FullyConstrained = true
  MakeInternals = false
  MapMode = 5
  Placement = pos=(56.1806,0,0) rot=(0.57735,-0.57735,-0.57735;2.0944rad)
  sketch-geometry (4):
    g0: LineSegment StartX=14.5251 StartY=6 StartZ=0 EndX=27.0787 EndY=6 EndZ=0
    g1: LineSegment StartX=20.8019 StartY=11 StartZ=0 EndX=20.8019 EndY=1 EndZ=0
    g2: GeomPoint [constr] X=20.8019 Y=6 Z=0
    g3: GeomPoint [constr] X=20.8019 Y=6 Z=0
  constraints (7):
    c: Coincident(g0,g-3)
    c: Coincident(g0,g-4)
    c: Vertical(g1)
    c: Symmetric(g0,g0,g2)
    c: Symmetric(g1,g1,g3)
    c: Coincident(g3,g2)
    c: DistanceY(g1,g1) = 10
FEATURE [PartDesign::Plane] DatumPlane
  AttachmentSupport = -> [Sketch024]
  Length = 124.385
  MapMode = 7
  Placement = pos=(56.1806,-20.8019,6) rot=(0,0.707107,0.707107;3.14159rad)
  ResizeMode = 0
  Width = 64.8041
FEATURE [PartDesign::Pocket] Pocket005  label="LED Hole"
  BaseFeature = -> Pad008
  Direction = (1,0,0)
  Length = 5
  Length2 = 5
  Profile = -> Sketch023
  ReferenceAxis = -> Sketch023 [N_Axis]
  Refine = true
  Suppressed = false
  Type = 2
FEATURE [PartDesign::Mirrored] Mirrored  label="LED Hole Mirror"
  BaseFeature = -> Pocket005
  MirrorPlane = -> DatumPlane
  Originals = -> [Pocket005]
  Refine = true
  Suppressed = false
  TransformMode = 0
FEATURE [PartDesign::SubShapeBinder] Binder007
  BindCopyOnChange = 0
  BindMode = 0
  ClaimChildren = false
  Context = -> Assembly [Part010.Body.Binder007.]
  Fuse = false
  MakeFace = true
  OffsetFill = false
  OffsetIntersection = false
  OffsetJoinType = 0
  OffsetOpenResult = false
  PartialLoad = false
  Refine = true
  Relative = true
  Support = -> [Part008[Body004.Pocket003.Face4]]
  _Version = 2
FEATURE [Sketcher::SketchObject] Sketch025
  ArcFitTolerance = 1e-06
  AttachmentSupport = -> [Mirrored]
  ExternalGeometry = -> [Binder007,Binder004]
  FullyConstrained = true
  MakeInternals = false
  MapMode = 5
  Placement = pos=(0,0,0) rot=(1,0,0;3.14159rad)
  sketch-geometry (17):
    g0: ArcOfCircle CenterX=80.7939 CenterY=14.5071 CenterZ=0 NormalX=0 NormalY=0 NormalZ=1 AngleXU=0 Radius=2.5 StartAngle=4.01697 EndAngle=8.54756
    g1: LineSegment StartX=79.1957 StartY=16.4295 StartZ=0 EndX=79.1922 EndY=12.5876 EndZ=0
    g2: Circle [constr] CenterX=80.7939 CenterY=14.5071 CenterZ=0 NormalX=0 NormalY=0 NormalZ=1 AngleXU=0 Radius=3.3
    g3: Circle [constr] CenterX=80.7939 CenterY=14.5071 CenterZ=0 NormalX=0 NormalY=0 NormalZ=1 AngleXU=0 Radius=4.1
    g4: ArcOfCircle CenterX=80.7939 CenterY=14.5071 CenterZ=0 NormalX=0 NormalY=0 NormalZ=1 AngleXU=0 Radius=3.3 StartAngle=3.83972 EndAngle=5.58505
    g5: ArcOfCircle CenterX=80.7939 CenterY=14.5071 CenterZ=0 NormalX=0 NormalY=0 NormalZ=1 AngleXU=0 Radius=4.1 StartAngle=3.83972 EndAngle=5.58505
    g6: LineSegment [constr] StartX=80.7939 StartY=14.5071 StartZ=0 EndX=76.6939 EndY=14.5071 EndZ=0
    g7: LineSegment [constr] StartX=80.7939 StartY=14.5071 StartZ=0 EndX=77.6531 EndY=17.1425 EndZ=0
    g8: LineSegment [constr] StartX=80.7939 StartY=14.5071 StartZ=0 EndX=83.9347 EndY=17.1425 EndZ=0
    g9: LineSegment [constr] StartX=80.7939 StartY=14.5071 StartZ=0 EndX=77.6531 EndY=11.8717 EndZ=0
    g10: LineSegment [constr] StartX=80.7939 StartY=14.5071 StartZ=0 EndX=83.9347 EndY=11.8717 EndZ=0
    g11: LineSegment StartX=77.6531 StartY=17.1425 StartZ=0 EndX=78.266 EndY=16.6283 EndZ=0
    g12: LineSegment StartX=83.9347 StartY=17.1425 StartZ=0 EndX=83.3219 EndY=16.6283 EndZ=0
    g13: LineSegment StartX=83.9347 StartY=11.8717 StartZ=0 EndX=83.3219 EndY=12.3859 EndZ=0
    g14: LineSegment StartX=77.6531 StartY=11.8717 StartZ=0 EndX=78.266 EndY=12.3859 EndZ=0
    g15: ArcOfCircle CenterX=80.7939 CenterY=14.5071 CenterZ=0 NormalX=0 NormalY=0 NormalZ=1 AngleXU=0 Radius=3.3 StartAngle=0.698132 EndAngle=2.44346
    g16: ArcOfCircle CenterX=80.7939 CenterY=14.5071 CenterZ=0 NormalX=0 NormalY=0 NormalZ=1 AngleXU=0 Radius=4.1 StartAngle=0.698132 EndAngle=2.44346
  constraints (49):
    c: Coincident(g0,g-3)
    c: Equal(g0,g-3)
    c: Parallel(g1,g-4)
    c: Distance(g1,g-4) = 0.4
    c: Coincident(g0,g1)
    c: Coincident(g0,g1)
    c: Coincident(g2,g0)
    c: Coincident(g3,g2)
    c: Coincident(g4,g2)
    c: Coincident(g5,g2)
    c: Distance(g0,g2) = 0.8
    c: Distance(g2,g3) = 0.8
    c: Coincident(g6,g0)
    c: Horizontal(g6)
    c: Coincident(g7,g0)
    c: Coincident(g8,g7)
    c: PointOnObject(g8,g16)
    c: Coincident(g9,g7)
    c: Coincident(g10,g7)
    c: Coincident(g11,g7)
    c: Coincident(g12,g8)
    c: PointOnObject(g12,g15)
    c: Coincident(g13,g10)
    c: PointOnObject(g13,g4)
    c: PointOnObject(g14,g4)
    c: Coincident(g14,g9)
    c: PointOnObject(g14,g9)
    c: PointOnObject(g13,g10)
    c: PointOnObject(g12,g8)
    c: PointOnObject(g11,g7)
    c: Angle(g7,g6) = 0.698132
    c: Angle(g6,g9) = 0.698132
    c: Angle(g8,g6) = 2.44346
    c: Angle(g6,g10) = 2.44346
    c: Coincident(g16,g7)
    c: Coincident(g15,g11)
    c: PointOnObject(g4,g9)
    c: Coincident(g5,g9)
    c: Equal(g4,g15)
    c: PointOnObject(g15,g8)
    c: Coincident(g4,g15)
    c: Equal(g5,g16)
    c: PointOnObject(g16,g8)
    c: Coincident(g5,g16)
    c: Coincident(g5,g10)
    c: PointOnObject(g4,g10)
    c: Equal(g16,g3)
    c: Equal(g15,g2)
    c: PointOnObject(g6,g3)
FEATURE [PartDesign::Pocket] Pocket006  label="PD Hole1"
  BaseFeature = -> Mirrored
  Direction = (0,0,1)
  Length = 0
  Length2 = 5
  Profile = -> Sketch025
  ReferenceAxis = -> Sketch025 [N_Axis]
  Refine = true
  Suppressed = false
  Type = 3
  UpToFace = -> Binder007 [Face1]
FEATURE [Sketcher::SketchObject] Sketch026
  ArcFitTolerance = 1e-06
  AttachmentSupport = -> [Pocket006]
  ExternalGeometry = -> [Binder004]
  FullyConstrained = true
  MakeInternals = false
  MapMode = 5
  Placement = pos=(76.6127,0,0) rot=(0.57735,-0.57735,-0.57735;2.0944rad)
  sketch-geometry (3):
    g0: LineSegment [constr] StartX=13.0082 StartY=7.5 StartZ=0 EndX=16.0082 EndY=4.5 EndZ=0
    g1: GeomPoint X=14.5082 Y=6 Z=0
    g2: Circle CenterX=14.5082 CenterY=6 CenterZ=0 NormalX=0 NormalY=0 NormalZ=1 AngleXU=0 Radius=2.37132
  constraints (5):
    c: Coincident(g0,g-5)
    c: Coincident(g0,g-6)
    c: Symmetric(g0,g0,g1)
    c: Coincident(g2,g1)
    c: Distance(g0,g2) = 0.25
FEATURE [PartDesign::Pocket] Pocket007  label="PD Hole2"
  BaseFeature = -> Pocket006
  Direction = (1,0,0)
  Length = 0
  Length2 = 5
  Profile = -> Sketch026
  ReferenceAxis = -> Sketch026 [N_Axis]
  Refine = true
  Suppressed = false
  Type = 3
  UpToFace = -> Pocket006 [Face34]
FEATURE [PartDesign::Mirrored] Mirrored001  label="PD Mirror"
  BaseFeature = -> Pocket007
  MirrorPlane = -> DatumPlane
  Originals = -> [Pocket006,Pocket007]
  Refine = true
  Suppressed = false
  TransformMode = 0
FEATURE [Sketcher::SketchObject] Sketch027
  ArcFitTolerance = 1e-06
  AttachmentSupport = -> [Mirrored001]
  ExternalGeometry = -> [Binder001]
  FullyConstrained = true
  MakeInternals = false
  MapMode = 5
  Placement = pos=(0,0,0) rot=(1,0,0;3.14159rad)
  sketch-geometry (3):
    g0: Circle CenterX=71.25 CenterY=37.5 CenterZ=0 NormalX=0 NormalY=0 NormalZ=1 AngleXU=0 Radius=1.1
    g1: Circle CenterX=80.5 CenterY=3.5 CenterZ=0 NormalX=0 NormalY=0 NormalZ=1 AngleXU=0 Radius=1.1
    g2: Circle CenterX=61.5 CenterY=3.5 CenterZ=0 NormalX=0 NormalY=0 NormalZ=1 AngleXU=0 Radius=1.1
  constraints (6):
    c: Coincident(g0,g-3)
    c: Equal(g0,g-3)
    c: Coincident(g1,g-5)
    c: Equal(g1,g-5)
    c: Coincident(g2,g-4)
    c: Equal(g2,g-4)
FEATURE [PartDesign::Pocket] Pocket008
  BaseFeature = -> Mirrored001
  Direction = (0,0,1)
  Length = 10
  Length2 = 5
  Profile = -> Sketch027
  ReferenceAxis = -> Sketch027 [N_Axis]
  Refine = true
  Suppressed = false
  Type = 0
FEATURE [Sketcher::SketchObject] Sketch028
  ArcFitTolerance = 1e-06
  AttachmentSupport = -> [Pocket008]
  ExternalGeometry = -> [Pocket008]
  FullyConstrained = true
  MakeInternals = false
  MapMode = 5
  Placement = pos=(84.5806,0,0) rot=(0.57735,0.57735,0.57735;2.0944rad)
  sketch-geometry (4):
    g0: LineSegment StartX=-40.0057 StartY=0 StartZ=0 EndX=-8.00566 EndY=0 EndZ=0
    g1: LineSegment StartX=-8.00566 StartY=0 StartZ=0 EndX=-8.00566 EndY=2 EndZ=0
    g2: LineSegment StartX=-8.00566 StartY=2 StartZ=0 EndX=-40.0057 EndY=2 EndZ=0
    g3: LineSegment StartX=-40.0057 StartY=2 StartZ=0 EndX=-40.0057 EndY=0 EndZ=0
  constraints (11):
    c: Coincident(g0,g1)
    c: Coincident(g1,g2)
    c: Coincident(g2,g3)
    c: Coincident(g3,g0)
    c: Horizontal(g0)
    c: Horizontal(g2)
    c: Vertical(g1)
    c: Vertical(g3)
    c: Coincident(g0,g-3)
    c: DistanceX(g2,g2) = 32
    c: DistanceY(g1,g1) = 2
FEATURE [PartDesign::Pocket] Pocket009
  BaseFeature = -> Pocket008
  Direction = (-1,0,0)
  Length = 10
  Length2 = 5
  Profile = -> Sketch028
  ReferenceAxis = -> Sketch028 [N_Axis]
  Refine = true
  Suppressed = false
  Type = 0
FEATURE [Sketcher::SketchObject] Sketch029
  ArcFitTolerance = 1e-06
  AttachmentSupport = -> [Pocket009]
  ExternalGeometry = -> [Pocket009]
  FullyConstrained = true
  MakeInternals = false
  MapMode = 5
  Placement = pos=(56.1806,0,0) rot=(0.57735,-0.57735,-0.57735;2.0944rad)
  sketch-geometry (4):
    g0: LineSegment StartX=40.0057 StartY=0 StartZ=0 EndX=40.0057 EndY=2 EndZ=0
    g1: LineSegment StartX=40.0057 StartY=2 StartZ=0 EndX=30.0057 EndY=2 EndZ=0
    g2: LineSegment StartX=30.0057 StartY=2 StartZ=0 EndX=30.0057 EndY=0 EndZ=0
    g3: LineSegment StartX=30.0057 StartY=0 StartZ=0 EndX=40.0057 EndY=0 EndZ=0
  constraints (11):
    c: Coincident(g0,g1)
    c: Coincident(g1,g2)
    c: Coincident(g2,g3)
    c: Coincident(g3,g0)
    c: Vertical(g0)
    c: Vertical(g2)
    c: Horizontal(g1)
    c: Horizontal(g3)
    c: Coincident(g0,g-3)
    c: DistanceX(g1,g1) = 10
    c: Distance(g2,g2) = 2
FEATURE [PartDesign::Pocket] Pocket010  label="ReliefSPI"
  BaseFeature = -> Pocket009
  Direction = (1,0,0)
  Length = 5
  Length2 = 5
  Profile = -> Sketch029
  ReferenceAxis = -> Sketch029 [N_Axis]
  Refine = true
  Suppressed = false
  Type = 0
FEATURE [PartDesign::Body] Body
  AllowCompound = false
  Group = -> [Binder,Binder001,Binder002,Binder003,Binder004,Binder007,Sketch,Pad,Sketch022,Pad008,Sketch023,Sketch024,DatumPlane,Pocket005,Mirrored,Sketch025,Pocket006,Sketch026,Pocket007,Mirrored001,Sketch027,Pocket008,Sketch028,Pocket009,Sketch029,Pocket010]
  Origin = -> Origin018
  Tip = -> Pocket010
COMPONENT P7 — recipe-attached ("Enclosure Back", modeled in this document).
Construction recipe (the document's own serialized feature program — sketch geometry with constraints, then the solid features built on it; lengths are millimeters unless a unit is written):

FEATURE [PartDesign::SubShapeBinder] Binder008
  BindCopyOnChange = 0
  BindMode = 0
  ClaimChildren = false
  Context = -> Assembly [Part011.Body006.Binder008.]
  Fuse = false
  MakeFace = true
  OffsetFill = false
  OffsetIntersection = false
  OffsetJoinType = 0
  OffsetOpenResult = false
  PartialLoad = false
  Refine = true
  Relative = true
  Support = -> [Board_bfa0[Pcb_bfa0.Face85]]
  _Version = 2
FEATURE [PartDesign::SubShapeBinder] Binder009
  BindCopyOnChange = 0
  BindMode = 0
  ClaimChildren = false
  Context = -> Assembly [Part011.Body006.Binder009.]
  Fuse = false
  MakeFace = true
  OffsetFill = false
  OffsetIntersection = false
  OffsetJoinType = 0
  OffsetOpenResult = false
  PartialLoad = false
  Refine = true
  Relative = true
  Support = -> [Part009[Body005.Pocket004.Face6]]
  _Version = 2
FEATURE [PartDesign::SubShapeBinder] Binder010
  BindCopyOnChange = 0
  BindMode = 0
  ClaimChildren = false
  Context = -> Assembly [Part011.Body006.Binder010.]
  Fuse = false
  MakeFace = true
  OffsetFill = false
  OffsetIntersection = false
  OffsetJoinType = 0
  OffsetOpenResult = false
  PartialLoad = false
  Refine = true
  Relative = true
  Support = -> [Part009[Body005.Pocket004.Face2]]
  _Version = 2
FEATURE [PartDesign::SubShapeBinder] Binder011
  BindCopyOnChange = 0
  BindMode = 0
  ClaimChildren = false
  Context = -> Assembly [Part011.Body006.Binder011.]
  Fuse = false
  MakeFace = true
  OffsetFill = false
  OffsetIntersection = false
  OffsetJoinType = 0
  OffsetOpenResult = false
  PartialLoad = false
  Refine = true
  Relative = true
  Support = -> [Part009[Body005.Pocket004.Face3]]
  _Version = 2
FEATURE [Sketcher::SketchObject] Sketch030
  ArcFitTolerance = 1e-06
  AttachmentSupport = -> [Binder008]
  ExternalGeometry = -> [Binder008]
  FullyConstrained = false
  MakeInternals = false
  MapMode = 5
  Placement = pos=(0,0,-1.6) rot=(1,0,0;3.14159rad)
  sketch-geometry (28):
    g0: Circle CenterX=3.5 CenterY=54.5 CenterZ=0 NormalX=0 NormalY=0 NormalZ=1 AngleXU=0 Radius=1.4
    g1: Circle CenterX=98 CenterY=54.5 CenterZ=0 NormalX=0 NormalY=0 NormalZ=1 AngleXU=0 Radius=1.4
    g2: Circle CenterX=98 CenterY=3.5 CenterZ=0 NormalX=0 NormalY=0 NormalZ=1 AngleXU=0 Radius=1.4
    g3: Circle CenterX=3.5 CenterY=3.5 CenterZ=0 NormalX=0 NormalY=0 NormalZ=1 AngleXU=0 Radius=1.4
    g4: LineSegment StartX=-2 StartY=52 StartZ=0 EndX=-2 EndY=6 EndZ=0
    g5: LineSegment StartX=103.5 StartY=6 StartZ=0 EndX=103.5 EndY=52 EndZ=0
    g6: LineSegment StartX=95.5 StartY=60 StartZ=0 EndX=6 EndY=60 EndZ=0
    g7: LineSegment StartX=-2 StartY=52 StartZ=0 EndX=6 EndY=52 EndZ=0
    g8: LineSegment StartX=6 StartY=52 StartZ=0 EndX=6 EndY=60 EndZ=0
    g9: LineSegment StartX=-2 StartY=6 StartZ=0 EndX=6 EndY=6 EndZ=0
    g10: LineSegment StartX=6 StartY=6 StartZ=0 EndX=6 EndY=-2 EndZ=0
    g11: LineSegment StartX=103.5 StartY=6 StartZ=0 EndX=95.5 EndY=6 EndZ=0
    g12: LineSegment StartX=95.5 StartY=6 StartZ=0 EndX=95.5 EndY=-2 EndZ=0
    g13: LineSegment StartX=103.5 StartY=52 StartZ=0 EndX=95.5 EndY=52 EndZ=0
    g14: LineSegment StartX=95.5 StartY=52 StartZ=0 EndX=95.5 EndY=60 EndZ=0
    g15: LineSegment StartX=-9 StartY=67 StartZ=0 EndX=-9 EndY=-9 EndZ=0
    g16: LineSegment StartX=-9 StartY=-9 StartZ=0 EndX=110.5 EndY=-9 EndZ=0
    g17: LineSegment StartX=110.5 StartY=-9 StartZ=0 EndX=110.5 EndY=67 EndZ=0
    g18: LineSegment StartX=110.5 StartY=67 StartZ=0 EndX=-9 EndY=67 EndZ=0
    g19: LineSegment [constr] StartX=6 StartY=60 StartZ=0 EndX=-28.0014 EndY=60 EndZ=0
    g20: LineSegment [constr] StartX=-2 StartY=59.8868 StartZ=0 EndX=-2 EndY=52 EndZ=0
    g21: LineSegment [constr] StartX=6 StartY=-2 StartZ=0 EndX=-2 EndY=-2 EndZ=0
    g22: LineSegment [constr] StartX=-2 StartY=-2 StartZ=0 EndX=-2 EndY=6 EndZ=0
    g23: LineSegment [constr] StartX=95.5 StartY=60 StartZ=0 EndX=103.5 EndY=60 EndZ=0
    g24: LineSegment [constr] StartX=103.5 StartY=60 StartZ=0 EndX=103.5 EndY=52 EndZ=0
    g25: LineSegment [constr] StartX=103.5 StartY=6 StartZ=0 EndX=103.5 EndY=-1.97275 EndZ=0
    g26: LineSegment [constr] StartX=103.5 StartY=-1.97275 StartZ=0 EndX=95.5 EndY=-1.97275 EndZ=0
    g27: LineSegment StartX=6 StartY=-2 StartZ=0 EndX=95.5 EndY=-2 EndZ=0
  constraints (74):
    c: Coincident(g0,g-3)
    c: Coincident(g1,g-9)
    c: Coincident(g2,g-8)
    c: Coincident(g-10,g3)
    c: Equal(g0,g3)
    c: Equal(g3,g2)
    c: Equal(g2,g1)
    c: Diameter(g0) = 2.8
    c: Vertical(g4)
    c: Vertical(g5)
    c: Horizontal(g6)
    c: Horizontal(g7)
    c: Coincident(g8,g7)
    c: Vertical(g8)
    c: Horizontal(g9)
    c: Coincident(g13,g14)
    c: Vertical(g14)
    c: Horizontal(g11)
    c: Vertical(g12)
    c: Coincident(g12,g11)
    c: Coincident(g9,g10)
    c: Vertical(g10)
    c: Equal(g7,g8)
    c: Equal(g8,g14)
    c: Equal(g14,g13)
    c: Equal(g13,g11)
    c: Equal(g11,g12)
    c: Equal(g12,g9)
    c: Equal(g9,g10)
    c: Distance(g8,g8) = 8
    c: Horizontal(g13)
    c: Coincident(g15,g16)
    c: Coincident(g16,g17)
    c: Coincident(g17,g18)
    c: Coincident(g18,g15)
    c: Vertical(g15)
    c: Vertical(g17)
    c: Horizontal(g16)
    c: Horizontal(g18)
    c: Coincident(g6,g8)
    c: Coincident(g4,g7)
    c: Coincident(g19,g6)
    c: Horizontal(g19)
    c: Coincident(g20,g4)
    c: Vertical(g20)
    c: Coincident(g21,g10)
    c: Coincident(g22,g21)
    c: Coincident(g22,g9)
    c: Coincident(g4,g9)
    c: Coincident(g5,g11)
    c: Coincident(g5,g13)
    c: Coincident(g6,g14)
    c: Coincident(g23,g6)
    c: Horizontal(g23)
    c: Coincident(g24,g23)
    c: Coincident(g24,g5)
    c: Coincident(g25,g5)
    c: Vertical(g25)
    c: Horizontal(g26)
    c: Coincident(g25,g26)
    c: Vertical(g24)
    c: Vertical(g22)
    c: Horizontal(g21)
    c: Distance(g6,g-4) = 2
    c: Distance(g4,g-5) = 2
    c: Distance(g15,g4) = 7
    c: Distance(g18,g6) = 7
    c: Distance(g5,g-6) = 2
    c: Distance(g17,g5) = 7
    c: Coincident(g27,g10)
    c: Coincident(g27,g12)
    c: Horizontal(g27)
    c: Distance(g27,g-7) = 2
    c: Distance(g16,g27) = 7
FEATURE [PartDesign::Pad] Pad009
  Direction = (0,0,-1)
  Length = 15
  Length2 = 10
  Profile = -> Sketch030
  ReferenceAxis = -> Sketch030 [N_Axis]
  Refine = true
  Suppressed = false
  Type = 0
FEATURE [Sketcher::SketchObject] Sketch031
  ArcFitTolerance = 1e-06
  AttachmentSupport = -> [Pad009]
  ExternalGeometry = -> [Pad009]
  FullyConstrained = true
  MakeInternals = false
  MapMode = 5
  Placement = pos=(0,0,-16.6) rot=(1,0,0;3.14159rad)
  sketch-geometry (4):
    g0: LineSegment StartX=-9 StartY=67 StartZ=0 EndX=-9 EndY=-9 EndZ=0
    g1: LineSegment StartX=-9 StartY=-9 StartZ=0 EndX=110.5 EndY=-9 EndZ=0
    g2: LineSegment StartX=110.5 StartY=-9 StartZ=0 EndX=110.5 EndY=67 EndZ=0
    g3: LineSegment StartX=110.5 StartY=67 StartZ=0 EndX=-9 EndY=67 EndZ=0
  constraints (10):
    c: Coincident(g0,g1)
    c: Coincident(g1,g2)
    c: Coincident(g2,g3)
    c: Coincident(g3,g0)
    c: Vertical(g0)
    c: Vertical(g2)
    c: Horizontal(g1)
    c: Horizontal(g3)
    c: Coincident(g0,g-3)
    c: Coincident(g1,g-4)
FEATURE [PartDesign::Pad] Pad010
  BaseFeature = -> Pad009
  Direction = (0,0,-1)
  Length = 7
  Length2 = 10
  Profile = -> Sketch031
  ReferenceAxis = -> Sketch031 [N_Axis]
  Refine = true
  Suppressed = false
  Type = 0
FEATURE [Sketcher::SketchObject] Sketch032
  ArcFitTolerance = 1e-06
  AttachmentSupport = -> [Pad010]
  ExternalGeometry = -> [Pad010,Binder008]
  FullyConstrained = true
  MakeInternals = false
  MapMode = 5
  Placement = pos=(0,9,0) rot=(0,0.707107,0.707107;3.14159rad)
  sketch-geometry (4):
    g0: LineSegment StartX=-25 StartY=-1.6 StartZ=0 EndX=-25 EndY=-12.6 EndZ=0
    g1: LineSegment StartX=-25 StartY=-12.6 StartZ=0 EndX=-13 EndY=-12.6 EndZ=0
    g2: LineSegment StartX=-13 StartY=-12.6 StartZ=0 EndX=-13 EndY=-1.6 EndZ=0
    g3: LineSegment StartX=-13 StartY=-1.6 StartZ=0 EndX=-25 EndY=-1.6 EndZ=0
  constraints (12):
    c: Coincident(g0,g1)
    c: Coincident(g1,g2)
    c: Coincident(g2,g3)
    c: Coincident(g3,g0)
    c: Vertical(g0)
    c: Vertical(g2)
    c: Horizontal(g1)
    c: Horizontal(g3)
    c: DistanceX(g1,g1) = 12
    c: Distance(g1,g-4) = 11
    c: Distance(g-2,g2) = 13
    c: PointOnObject(g2,g-4)
FEATURE [PartDesign::Pocket] Pocket011
  BaseFeature = -> Pad010
  Direction = (0,-1,2e-16)
  Length = 5
  Length2 = 5
  Profile = -> Sketch032
  ReferenceAxis = -> Sketch032 [N_Axis]
  Refine = true
  Suppressed = false
  Type = 2
FEATURE [Sketcher::SketchObject] Sketch036
  ArcFitTolerance = 1e-06
  AttachmentSupport = -> [Pocket011]
  ExternalGeometry = -> [Pocket011]
  FullyConstrained = false
  MakeInternals = false
  MapMode = 5
  Placement = pos=(0,0,-23.6) rot=(1,0,0;3.14159rad)
  sketch-geometry (17):
    g0: LineSegment [constr] StartX=6 StartY=60 StartZ=0 EndX=-2 EndY=60 EndZ=0
    g1: LineSegment [constr] StartX=-2 StartY=52 StartZ=0 EndX=-2 EndY=60 EndZ=0
    g2: LineSegment [constr] StartX=95.5 StartY=60 StartZ=0 EndX=103.5 EndY=60 EndZ=0
    g3: LineSegment [constr] StartX=103.5 StartY=52 StartZ=0 EndX=103.5 EndY=60 EndZ=0
    g4: LineSegment [constr] StartX=103.5 StartY=6 StartZ=0 EndX=103.5 EndY=-2 EndZ=0
    g5: LineSegment [constr] StartX=95.5 StartY=-2 StartZ=0 EndX=103.5 EndY=-2 EndZ=0
    g6: LineSegment [constr] StartX=25 StartY=-2 StartZ=0 EndX=-2 EndY=-2 EndZ=0
    g7: LineSegment [constr] StartX=-2 StartY=6 StartZ=0 EndX=-2 EndY=-2 EndZ=0
    g8: GeomPoint X=-2 Y=60 Z=0
    g9: LineSegment [constr] StartX=-2 StartY=60 StartZ=0 EndX=-2 EndY=-2 EndZ=0
    g10: LineSegment [constr] StartX=-2 StartY=-2 StartZ=0 EndX=103.5 EndY=-2 EndZ=0
    g11: LineSegment [constr] StartX=103.5 StartY=-2 StartZ=0 EndX=103.5 EndY=60 EndZ=0
    g12: LineSegment [constr] StartX=103.5 StartY=60 StartZ=0 EndX=-2 EndY=60 EndZ=0
    g13: Circle CenterX=-2 CenterY=60 CenterZ=0 NormalX=0 NormalY=0 NormalZ=1 AngleXU=0 Radius=1.73566
    g14: Circle CenterX=103.5 CenterY=60 CenterZ=0 NormalX=0 NormalY=0 NormalZ=1 AngleXU=0 Radius=2.15156
    g15: Circle CenterX=103.5 CenterY=-2 CenterZ=0 NormalX=0 NormalY=0 NormalZ=1 AngleXU=0 Radius=1.49444
    g16: Circle CenterX=-2 CenterY=-2 CenterZ=0 NormalX=0 NormalY=0 NormalZ=1 AngleXU=0 Radius=1.09035
  constraints (35):
    c: Coincident(g0,g-9)
    c: Horizontal(g0)
    c: Coincident(g1,g-10)
    c: Coincident(g1,g0)
    c: Vertical(g1)
    c: Coincident(g2,g-9)
    c: Horizontal(g2)
    c: Coincident(g3,g-8)
    c: Coincident(g3,g2)
    c: Vertical(g3)
    c: Coincident(g4,g-8)
    c: Vertical(g4)
    c: Coincident(g5,g-7)
    c: Coincident(g5,g4)
    c: Horizontal(g5)
    c: Coincident(g6,g-7)
    c: Horizontal(g6)
    c: Coincident(g7,g-10)
    c: Coincident(g7,g6)
    c: Vertical(g7)
    c: Coincident(g8,g0)
    c: Coincident(g9,g10)
    c: Coincident(g10,g11)
    c: Coincident(g11,g12)
    c: Coincident(g12,g9)
    c: Vertical(g9)
    c: Vertical(g11)
    c: Horizontal(g10)
    c: Horizontal(g12)
    c: Coincident(g13,g9)
    c: Coincident(g14,g11)
    c: Coincident(g15,g10)
    c: Coincident(g16,g9)
    c: Coincident(g0,g9)
    c: Coincident(g10,g4)
FEATURE [PartDesign::Hole] Hole
  BaseFeature = -> Pocket011
  CustomThreadClearance = 0
  Depth = 289.504
  DepthType = 1
  Diameter = 3.4
  DrillForDepth = false
  DrillPoint = 1
  DrillPointAngle = 118
  HoleCutCountersinkAngle = 90
  HoleCutCustomValues = false
  HoleCutDepth = 3.4
  HoleCutDiameter = 6.1
  HoleCutType = 1
  ModelThread = false
  Profile = -> Sketch036
  Refine = true
  Suppressed = false
  Tapered = false
  TaperedAngle = 90
  ThreadClass = 0
  ThreadDepth = 289.504
  ThreadDepthType = 0
  ThreadDirection = 0
  ThreadFit = 0
  ThreadSize = 9
  ThreadType = 1
  Threaded = false
  UseCustomThreadClearance = false
FEATURE [Sketcher::SketchObject] Sketch038
  ArcFitTolerance = 1e-06
  AttachmentSupport = -> [Hole]
  ExternalGeometry = -> [Binder009,Hole]
  FullyConstrained = true
  MakeInternals = false
  MapMode = 5
  Placement = pos=(0,0,-1.6) rot=(0,0,1;0rad)
  sketch-geometry (4):
    g0: LineSegment StartX=81.5715 StartY=9 StartZ=0 EndX=59.1715 EndY=9 EndZ=0
    g1: LineSegment StartX=59.1715 StartY=9 StartZ=0 EndX=56.2847 EndY=14 EndZ=0
    g2: LineSegment StartX=56.2847 StartY=14 StartZ=0 EndX=84.4582 EndY=14 EndZ=0
    g3: LineSegment StartX=84.4582 StartY=14 StartZ=0 EndX=81.5715 EndY=9 EndZ=0
  constraints (12):
    c: PointOnObject(g0,g-4)
    c: PointOnObject(g0,g-4)
    c: Coincident(g1,g0)
    c: Horizontal(g2)
    c: Coincident(g3,g2)
    c: Coincident(g3,g0)
    c: DistanceX(g-3,g0) = 5
    c: DistanceX(g0,g-3) = 5
    c: Angle(g1,g-4) = 1.0472
    c: Angle(g-4,g3) = 1.0472
    c: Distance(g0,g2) = 5
    c: Coincident(g1,g2)
FEATURE [PartDesign::Pad] Pad013
  BaseFeature = -> Hole
  Direction = (0,0,1)
  Length = 10
  Length2 = 10
  Profile = -> Sketch038
  ReferenceAxis = -> Sketch038 [N_Axis]
  Refine = true
  Reversed = true
  Suppressed = false
  Type = 3
  UpToFace = -> Hole [Face28]
FEATURE [PartDesign::Chamfer] Chamfer001
  Angle = 5
  Base = -> Pad013 [Edge71,Edge65]
  BaseFeature = -> Pad013
  ChamferType = 2
  FlipDirection = false
  Refine = true
  Size = 21
  Size2 = 1
  SupportTransform = false
  Suppressed = false
  UseAllEdges = false
FEATURE [PartDesign::Chamfer] Chamfer003
  Angle = 45
  Base = -> Chamfer001 [Edge67,Edge20,Edge68,Edge21,Edge5,Edge16,Edge56]
  BaseFeature = -> Chamfer001
  ChamferType = 0
  FlipDirection = false
  Refine = true
  Size = 3
  Size2 = 1
  SupportTransform = false
  Suppressed = false
  UseAllEdges = false
FEATURE [PartDesign::Chamfer] Chamfer004
  Angle = 45
  Base = -> Chamfer003 [Edge1,Edge17]
  BaseFeature = -> Chamfer003
  ChamferType = 0
  FlipDirection = false
  Refine = true
  Size = 1
  Size2 = 1
  SupportTransform = false
  Suppressed = false
  UseAllEdges = false
FEATURE [PartDesign::Chamfer] Chamfer005
  Angle = 45
  Base = -> Chamfer004 [Edge5,Edge7,Edge9]
  BaseFeature = -> Chamfer004
  ChamferType = 0
  FlipDirection = false
  Refine = true
  Size = 1
  Size2 = 1
  SupportTransform = false
  Suppressed = false
  UseAllEdges = false
FEATURE [PartDesign::Body] Body006
  AllowCompound = false
  Group = -> [Binder008,Binder009,Binder010,Binder011,Sketch030,Pad009,Sketch031,Pad010,Sketch032,Pocket011,Sketch036,Hole,Sketch038,Pad013,Chamfer001,Chamfer003,Chamfer004,Chamfer005]
  Origin = -> Origin020
  Tip = -> Chamfer005
COMPONENT P8 — recipe-attached ("Enclosure Front", modeled in this document).
Construction recipe (the document's own serialized feature program — sketch geometry with constraints, then the solid features built on it; lengths are millimeters unless a unit is written):

FEATURE [PartDesign::SubShapeBinder] Binder012
  BindCopyOnChange = 0
  BindMode = 0
  ClaimChildren = false
  Context = -> Assembly [Part012.Body007.Binder012.]
  Fuse = false
  MakeFace = true
  OffsetFill = false
  OffsetIntersection = false
  OffsetJoinType = 0
  OffsetOpenResult = false
  PartialLoad = false
  Refine = true
  Relative = true
  Support = -> [Part011[Body006.Pocket011.]]
  _Version = 2
FEATURE [PartDesign::SubShapeBinder] Binder013
  BindCopyOnChange = 0
  BindMode = 0
  ClaimChildren = false
  Context = -> Assembly [Part012.Body007.Binder013.]
  Fuse = false
  MakeFace = true
  OffsetFill = false
  OffsetIntersection = false
  OffsetJoinType = 0
  OffsetOpenResult = false
  PartialLoad = false
  Refine = true
  Relative = true
  Support = -> [Part009[Body005.Pocket004.Face1]]
  _Version = 2
FEATURE [PartDesign::SubShapeBinder] Binder014
  BindCopyOnChange = 0
  BindMode = 0
  ClaimChildren = false
  Context = -> Assembly [Part012.Body007.Binder014.]
  Fuse = false
  MakeFace = true
  OffsetFill = false
  OffsetIntersection = false
  OffsetJoinType = 0
  OffsetOpenResult = false
  PartialLoad = false
  Refine = true
  Relative = true
  Support = -> [Part009[Body005.Pocket004.Face2]]
  _Version = 2
FEATURE [PartDesign::SubShapeBinder] Binder015
  BindCopyOnChange = 0
  BindMode = 0
  ClaimChildren = false
  Context = -> Assembly [Part012.Body007.Binder015.]
  Fuse = false
  MakeFace = true
  OffsetFill = false
  OffsetIntersection = false
  OffsetJoinType = 0
  OffsetOpenResult = false
  PartialLoad = false
  Refine = true
  Relative = true
  Support = -> [Part009[Body005.Pocket004.Face3]]
  _Version = 2
FEATURE [Sketcher::SketchObject] Sketch033
  ArcFitTolerance = 1e-06
  AttachmentSupport = -> [Binder012]
  ExternalGeometry = -> [Binder012]
  FullyConstrained = true
  MakeInternals = false
  MapMode = 5
  Placement = pos=(0,0,-1.6) rot=(0,0,1;0rad)
  sketch-geometry (16):
    g0: LineSegment StartX=-9 StartY=9 StartZ=0 EndX=-9 EndY=-67 EndZ=0
    g1: LineSegment StartX=-9 StartY=-67 StartZ=0 EndX=110.5 EndY=-67 EndZ=0
    g2: LineSegment StartX=110.5 StartY=-67 StartZ=0 EndX=110.5 EndY=9 EndZ=0
    g3: LineSegment StartX=110.5 StartY=9 StartZ=0 EndX=-9 EndY=9 EndZ=0
    g4: LineSegment StartX=103.5 StartY=-60 StartZ=0 EndX=103.5 EndY=2 EndZ=0
    g5: LineSegment StartX=103.5 StartY=2 StartZ=0 EndX=-2 EndY=2 EndZ=0
    g6: LineSegment StartX=-2 StartY=2 StartZ=0 EndX=-2 EndY=-60 EndZ=0
    g7: LineSegment StartX=-2 StartY=-60 StartZ=0 EndX=103.5 EndY=-60 EndZ=0
    g8: LineSegment [constr] StartX=6 StartY=2 StartZ=0 EndX=-2 EndY=2 EndZ=0
    g9: LineSegment [constr] StartX=-2 StartY=-6 StartZ=0 EndX=-2 EndY=2 EndZ=0
    g10: LineSegment [constr] StartX=95.5 StartY=2 StartZ=0 EndX=103.5 EndY=2 EndZ=0
    g11: LineSegment [constr] StartX=103.5 StartY=2 StartZ=0 EndX=103.5 EndY=-6 EndZ=0
    g12: LineSegment [constr] StartX=103.5 StartY=-52 StartZ=0 EndX=103.5 EndY=-60 EndZ=0
    g13: LineSegment [constr] StartX=95.5 StartY=-60 StartZ=0 EndX=103.5 EndY=-60 EndZ=0
    g14: LineSegment [constr] StartX=-2 StartY=-52 StartZ=0 EndX=-2 EndY=-60 EndZ=0
    g15: LineSegment [constr] StartX=6 StartY=-60 StartZ=0 EndX=-2 EndY=-60 EndZ=0
  constraints (40):
    c: Coincident(g0,g1)
    c: Coincident(g1,g2)
    c: Coincident(g2,g3)
    c: Coincident(g3,g0)
    c: Vertical(g0)
    c: Vertical(g2)
    c: Horizontal(g1)
    c: Horizontal(g3)
    c: Coincident(g0,g-4)
    c: Coincident(g1,g-6)
    c: Coincident(g4,g5)
    c: Coincident(g5,g6)
    c: Coincident(g6,g7)
    c: Coincident(g7,g4)
    c: Vertical(g4)
    c: Vertical(g6)
    c: Horizontal(g5)
    c: Horizontal(g7)
    c: Coincident(g8,g-7)
    c: Horizontal(g8)
    c: Coincident(g9,g-8)
    c: Coincident(g9,g8)
    c: Vertical(g9)
    c: Coincident(g10,g-7)
    c: Horizontal(g10)
    c: Coincident(g11,g10)
    c: Coincident(g11,g-10)
    c: Vertical(g11)
    c: Coincident(g12,g-10)
    c: Vertical(g12)
    c: Coincident(g13,g-9)
    c: Coincident(g13,g12)
    c: Horizontal(g13)
    c: Coincident(g14,g-8)
    c: Vertical(g14)
    c: Coincident(g15,g-9)
    c: Coincident(g15,g14)
    c: Horizontal(g15)
    c: Coincident(g14,g6)
    c: Coincident(g4,g10)
FEATURE [PartDesign::Pad] Pad011
  Direction = (0,0,1)
  Length = 20
  Length2 = 10
  Profile = -> Sketch033
  ReferenceAxis = -> Sketch033 [N_Axis]
  Refine = true
  Suppressed = false
  Type = 0
FEATURE [Sketcher::SketchObject] Sketch034
  ArcFitTolerance = 1e-06
  AttachmentSupport = -> [Pad011]
  ExternalGeometry = -> [Pad011]
  FullyConstrained = true
  MakeInternals = false
  MapMode = 5
  Placement = pos=(0,0,18.4) rot=(0,0,1;0rad)
  sketch-geometry (4):
    g0: LineSegment StartX=-9 StartY=9 StartZ=0 EndX=-9 EndY=-67 EndZ=0
    g1: LineSegment StartX=-9 StartY=-67 StartZ=0 EndX=110.5 EndY=-67 EndZ=0
    g2: LineSegment StartX=110.5 StartY=-67 StartZ=0 EndX=110.5 EndY=9 EndZ=0
    g3: LineSegment StartX=110.5 StartY=9 StartZ=0 EndX=-9 EndY=9 EndZ=0
  constraints (10):
    c: Coincident(g0,g1)
    c: Coincident(g1,g2)
    c: Coincident(g2,g3)
    c: Coincident(g3,g0)
    c: Vertical(g0)
    c: Vertical(g2)
    c: Horizontal(g1)
    c: Horizontal(g3)
    c: Coincident(g0,g-3)
    c: Coincident(g1,g-4)
FEATURE [PartDesign::Pad] Pad012
  BaseFeature = -> Pad011
  Direction = (0,0,1)
  Length = 7
  Length2 = 10
  Profile = -> Sketch034
  ReferenceAxis = -> Sketch034 [N_Axis]
  Refine = true
  Suppressed = false
  Type = 0
FEATURE [Sketcher::SketchObject] Sketch035
  ArcFitTolerance = 1e-06
  AttachmentSupport = -> [Pad012]
  ExternalGeometry = -> [Binder013,Binder015,Binder014,Pad012]
  FullyConstrained = true
  MakeInternals = false
  MapMode = 5
  Placement = pos=(0,9,0) rot=(0,0.707107,0.707107;3.14159rad)
  sketch-geometry (4):
    g0: LineSegment StartX=-76.5715 StartY=12.4 StartZ=0 EndX=-76.5715 EndY=-1.6 EndZ=0
    g1: LineSegment StartX=-76.5715 StartY=-1.6 StartZ=0 EndX=-64.1715 EndY=-1.6 EndZ=0
    g2: LineSegment StartX=-64.1715 StartY=-1.6 StartZ=0 EndX=-64.1715 EndY=12.4 EndZ=0
    g3: LineSegment StartX=-64.1715 StartY=12.4 StartZ=0 EndX=-76.5715 EndY=12.4 EndZ=0
  constraints (11):
    c: Coincident(g0,g1)
    c: Coincident(g1,g2)
    c: Coincident(g2,g3)
    c: Coincident(g3,g0)
    c: Vertical(g0)
    c: Vertical(g2)
    c: Horizontal(g1)
    c: Horizontal(g3)
    c: Coincident(g0,g-4)
    c: PointOnObject(g1,g-6)
    c: PointOnObject(g-5,g2)
FEATURE [PartDesign::Pocket] Pocket012
  BaseFeature = -> Pad012
  Direction = (0,-1,2e-16)
  Length = 5
  Length2 = 5
  Profile = -> Sketch035
  ReferenceAxis = -> Sketch035 [N_Axis]
  Refine = true
  Suppressed = false
  Type = 2
FEATURE [PartDesign::Chamfer] Chamfer
  Angle = 45
  Base = -> Pocket012 [Edge17,Edge16,Edge18]
  BaseFeature = -> Pocket012
  ChamferType = 0
  FlipDirection = false
  Refine = true
  Size = 6
  Size2 = 1
  SupportTransform = false
  Suppressed = false
  UseAllEdges = false
FEATURE [PartDesign::SubShapeBinder] Binder016
  BindCopyOnChange = 0
  BindMode = 0
  ClaimChildren = false
  Context = -> Assembly [Part012.Body007.Binder016.]
  Fuse = false
  MakeFace = true
  OffsetFill = false
  OffsetIntersection = false
  OffsetJoinType = 0
  OffsetOpenResult = false
  PartialLoad = false
  Refine = true
  Relative = true
  Support = -> [Part011[Body006.Hole.Face1]]
  _Version = 2
FEATURE [PartDesign::Fillet] Fillet
  Base = -> Chamfer [Edge33,Edge31,Edge35,Edge37]
  BaseFeature = -> Chamfer
  Radius = 7
  Refine = true
  SupportTransform = false
  Suppressed = false
  UseAllEdges = false
FEATURE [Sketcher::SketchObject] Sketch037
  ArcFitTolerance = 1e-06
  AttachmentSupport = -> [Fillet]
  ExternalGeometry = -> [Binder016]
  FullyConstrained = true
  MakeInternals = false
  MapMode = 5
  Placement = pos=(0,0,-1.6) rot=(1,0,0;3.14159rad)
  sketch-geometry (4):
    g0: Circle CenterX=-2 CenterY=60 CenterZ=0 NormalX=0 NormalY=0 NormalZ=1 AngleXU=0 Radius=1.45
    g1: Circle CenterX=103.5 CenterY=60 CenterZ=0 NormalX=0 NormalY=0 NormalZ=1 AngleXU=0 Radius=1.45
    g2: Circle CenterX=103.5 CenterY=-2 CenterZ=0 NormalX=0 NormalY=0 NormalZ=1 AngleXU=0 Radius=1.45
    g3: Circle CenterX=-2 CenterY=-2 CenterZ=0 NormalX=0 NormalY=0 NormalZ=1 AngleXU=0 Radius=1.45
  constraints (8):
    c: Coincident(g0,g-3)
    c: Coincident(g1,g-4)
    c: Coincident(g2,g-5)
    c: Coincident(g3,g-6)
    c: Equal(g3,g0)
    c: Equal(g0,g1)
    c: Equal(g1,g2)
    c: Diameter(g2) = 2.9
FEATURE [PartDesign::Pocket] Pocket013
  BaseFeature = -> Fillet
  Direction = (0,0,1)
  Length = 15
  Length2 = 5
  Profile = -> Sketch037
  ReferenceAxis = -> Sketch037 [N_Axis]
  Refine = true
  Suppressed = false
  Type = 0
FEATURE [PartDesign::Chamfer] Chamfer006
  Angle = 45
  Base = -> Pocket013 [Edge43,Edge41,Edge54,Edge50,Edge51,Edge39,Edge47,Edge46]
  BaseFeature = -> Pocket013
  ChamferType = 0
  FlipDirection = false
  Refine = true
  Size = 3
  Size2 = 1
  SupportTransform = false
  Suppressed = false
  UseAllEdges = false
FEATURE [PartDesign::Body] Body007
  AllowCompound = false
  Group = -> [Binder012,Binder013,Binder014,Binder015,Sketch033,Pad011,Sketch034,Pad012,Sketch035,Pocket012,Chamfer,Binder016,Fillet,Sketch037,Pocket013,Chamfer006]
  Origin = -> Origin022
  Tip = -> Chamfer006
COMPONENT P9 — recipe-attached ("Enclosure Cap", modeled in this document).
Construction recipe (the document's own serialized feature program — sketch geometry with constraints, then the solid features built on it; lengths are millimeters unless a unit is written):

FEATURE [PartDesign::SubShapeBinder] Binder017
  BindCopyOnChange = 0
  BindMode = 0
  ClaimChildren = false
  Context = -> Assembly [Part013.Body008.Binder017.]
  Fuse = false
  MakeFace = true
  OffsetFill = false
  OffsetIntersection = false
  OffsetJoinType = 0
  OffsetOpenResult = false
  PartialLoad = false
  Refine = true
  Relative = true
  Support = -> [Part012[Body007.Pocket013.Face25]]
  _Version = 2
FEATURE [PartDesign::SubShapeBinder] Binder018
  BindCopyOnChange = 0
  BindMode = 0
  ClaimChildren = false
  Context = -> Assembly [Part013.Body008.Binder018.]
  Fuse = false
  MakeFace = true
  OffsetFill = false
  OffsetIntersection = false
  OffsetJoinType = 0
  OffsetOpenResult = false
  PartialLoad = false
  Refine = true
  Relative = true
  Support = -> [Part011[Body006.Chamfer001.Face5]]
  _Version = 2
FEATURE [Sketcher::SketchObject] Sketch039
  ArcFitTolerance = 1e-06
  AttachmentSupport = -> [Binder017]
  ExternalGeometry = -> [Binder017,Binder018]
  FullyConstrained = true
  MakeInternals = false
  MapMode = 5
  Placement = pos=(0,0,25.4) rot=(0,0,1;0rad)
  sketch-geometry (4):
    g0: LineSegment StartX=53.4062 StartY=9 StartZ=0 EndX=87.3367 EndY=9 EndZ=0
    g1: LineSegment StartX=87.3367 StartY=9 StartZ=0 EndX=87.3367 EndY=20 EndZ=0
    g2: LineSegment StartX=87.3367 StartY=20 StartZ=0 EndX=53.4062 EndY=20 EndZ=0
    g3: LineSegment StartX=53.4062 StartY=20 StartZ=0 EndX=53.4062 EndY=9 EndZ=0
  constraints (12):
    c: Coincident(g0,g1)
    c: Coincident(g1,g2)
    c: Coincident(g2,g3)
    c: Coincident(g3,g0)
    c: Horizontal(g0)
    c: Horizontal(g2)
    c: Vertical(g1)
    c: Vertical(g3)
    c: Distance(g2,g-4) = 6
    c: Distance(g-4,g1) = 5
    c: Distance(g-4,g3) = 5
    c: PointOnObject(g0,g-3)
FEATURE [PartDesign::Pad] Pad014
  Direction = (0,0,1)
  Length = 48
  Length2 = 10
  Profile = -> Sketch039
  ReferenceAxis = -> Sketch039 [N_Axis]
  Refine = true
  Reversed = true
  Suppressed = false
  Type = 0
FEATURE [PartDesign::SubShapeBinder] Binder019
  BindCopyOnChange = 0
  BindMode = 0
  ClaimChildren = false
  Context = -> Assembly [Part013.Body008.Binder019.]
  Fuse = false
  MakeFace = true
  OffsetFill = false
  OffsetIntersection = false
  OffsetJoinType = 0
  OffsetOpenResult = false
  PartialLoad = false
  Refine = true
  Relative = true
  Support = -> [Part011[Body006.Chamfer001.Face4]]
  _Version = 2
FEATURE [Sketcher::SketchObject] Sketch040
  ArcFitTolerance = 1e-06
  AttachmentSupport = -> [Binder018]
  ExternalGeometry = -> [Binder018]
  FullyConstrained = true
  MakeInternals = false
  MapMode = 5
  Placement = pos=(0,0,-1.6) rot=(0,0,1;0rad)
  sketch-geometry (4):
    g0: LineSegment StartX=58.4062 StartY=14 StartZ=0 EndX=82.3367 EndY=14 EndZ=0
    g1: LineSegment StartX=82.3367 StartY=14 StartZ=0 EndX=79.45 EndY=9 EndZ=0
    g2: LineSegment StartX=79.45 StartY=9 StartZ=0 EndX=61.293 EndY=9 EndZ=0
    g3: LineSegment StartX=61.293 StartY=9 StartZ=0 EndX=58.4062 EndY=14 EndZ=0
  constraints (8):
    c: Coincident(g0,g-4)
    c: Coincident(g1,g0)
    c: Coincident(g1,g-5)
    c: Coincident(g2,g1)
    c: Coincident(g2,g-4)
    c: Coincident(g3,g2)
    c: Coincident(g3,g0)
    c: Coincident(g-5,g0)
FEATURE [Sketcher::SketchObject] Sketch041
  ArcFitTolerance = 1e-06
  AttachmentSupport = -> [Binder019]
  ExternalGeometry = -> [Binder019]
  FullyConstrained = true
  MakeInternals = false
  MapMode = 5
  Placement = pos=(0,0,-23.6) rot=(1,0,0;3.14159rad)
  sketch-geometry (4):
    g0: LineSegment StartX=56.2847 StartY=-14 StartZ=0 EndX=84.4582 EndY=-14 EndZ=0
    g1: LineSegment StartX=84.4582 StartY=-14 StartZ=0 EndX=81.5715 EndY=-9 EndZ=0
    g2: LineSegment StartX=81.5715 StartY=-9 StartZ=0 EndX=59.1715 EndY=-9 EndZ=0
    g3: LineSegment StartX=59.1715 StartY=-9 StartZ=0 EndX=56.2847 EndY=-14 EndZ=0
  constraints (8):
    c: Coincident(g0,g-5)
    c: Coincident(g0,g-4)
    c: Coincident(g1,g0)
    c: Coincident(g1,g-4)
    c: Coincident(g2,g1)
    c: Coincident(g2,g-5)
    c: Coincident(g3,g2)
    c: Coincident(g3,g0)
FEATURE [PartDesign::SubtractiveLoft] SubtractiveLoft
  BaseFeature = -> Pad014
  Closed = false
  Profile = -> Sketch041
  Refine = true
  Ruled = false
  Sections = -> [Sketch040]
  Suppressed = false
FEATURE [PartDesign::Pocket] Pocket014
  BaseFeature = -> SubtractiveLoft
  Direction = (0,0,1)
  Length = 15
  Length2 = 5
  Profile = -> SubtractiveLoft [Face6]
  Refine = true
  Suppressed = false
  Type = 0
FEATURE [PartDesign::Chamfer] Chamfer002
  Angle = 45
  Base = -> Pocket014 [Edge11,Edge14,Edge12,Edge13,Edge30,Edge16,Edge17,Edge15]
  BaseFeature = -> Pocket014
  ChamferType = 0
  FlipDirection = false
  Refine = true
  Size = 2
  Size2 = 1
  SupportTransform = false
  Suppressed = false
  UseAllEdges = false
FEATURE [PartDesign::Body] Body008
  AllowCompound = false
  Group = -> [Binder018,Binder017,Sketch039,Pad014,Binder019,Sketch040,Sketch041,SubtractiveLoft,Pocket014,Chamfer002]
  Origin = -> Origin024
  Tip = -> Chamfer002
PROVENANCE & LICENSES
A FreeCAD (.FCStd) document from a public repository crawl; recipes are the document's own serialized feature recipes (and, for linked parts, companion documents' recipes).
License: cern-ohl.
